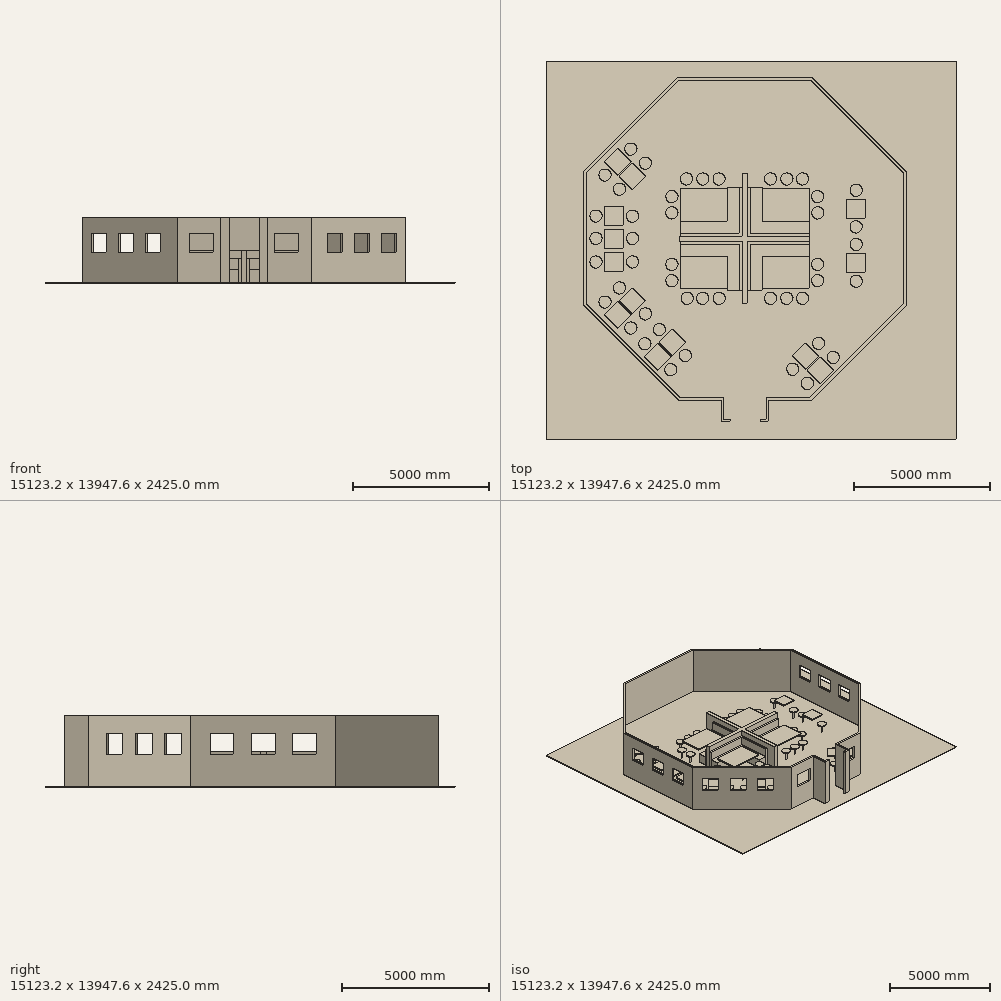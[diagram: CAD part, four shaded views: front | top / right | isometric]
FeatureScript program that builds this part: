
annotation { "Feature Type Name" : "Feature", "Feature Type Description" : "" }
export const myFeature = defineFeature(function(context is Context, id is Id, definition is map)
    precondition{}
    {
        {
            var Q0;
            Q0=qCreatedBy(makeId("Top.planeOp"),FACE);
            var sketch = newSketch(context, id + "F0", { "sketchPlane" : qUnion([Q0])});
            skLineSegment(sketch, "E0", {"start": v(-5845, -1966.08) * mm, "end": v(-2421.08, -5390) * mm});
            skLineSegment(sketch, "E1", {"start": v(-2421.08, -5390) * mm, "end": v(-780, -5390) * mm});
            skLineSegment(sketch, "E2", {"start": v(2421.08, -5390) * mm, "end": v(5845, -1966.08) * mm});
            skLineSegment(sketch, "E3", {"start": v(5845, -1966.08) * mm, "end": v(5845, 2876.08) * mm});
            skLineSegment(sketch, "E4", {"start": v(5845, 2876.08) * mm, "end": v(2421.08, 6300) * mm});
            skLineSegment(sketch, "E5", {"start": v(2421.08, 6300) * mm, "end": v(-2421.08, 6300) * mm});
            skLineSegment(sketch, "E6", {"start": v(-5955, -2011.64) * mm, "end": v(-2466.64, -5500) * mm});
            skLineSegment(sketch, "E7", {"start": v(-2466.64, -5500) * mm, "end": v(-870, -5500) * mm});
            skLineSegment(sketch, "E8", {"start": v(2466.64, -5500) * mm, "end": v(5955, -2011.64) * mm});
            skLineSegment(sketch, "E9", {"start": v(5955, -2011.64) * mm, "end": v(5955, 2921.64) * mm});
            skLineSegment(sketch, "E10", {"start": v(5955, 2921.64) * mm, "end": v(2466.64, 6410) * mm});
            skLineSegment(sketch, "E11", {"start": v(2466.64, 6410) * mm, "end": v(-2466.64, 6410) * mm});
            skLineSegment(sketch, "E12", {"start": v(-2466.64, 6410) * mm, "end": v(-5955, 2921.64) * mm});
            skLineSegment(sketch, "E13", {"start": v(-5955, 2921.64) * mm, "end": v(-5955, -2011.64) * mm});
            skLineSegment(sketch, "E14", {"start": v(-5845, 2876.08) * mm, "end": v(-5845, -1966.08) * mm});
            skLineSegment(sketch, "E15", {"start": v(4545, -1427.6) * mm, "end": v(4545, 2337.6) * mm});
            skLineSegment(sketch, "E16", {"start": v(4545, 2337.6) * mm, "end": v(3837.9, 3044.7) * mm});
            skLineSegment(sketch, "E17", {"start": v(4403.58, -1569.02) * mm, "end": v(4545, -1427.6) * mm});
            skLineSegment(sketch, "E18", {"start": v(5845, 2876.08) * mm, "end": v(4545, 2337.6) * mm});
            skLineSegment(sketch, "E19", {"start": v(5845, -1966.08) * mm, "end": v(4545, -1427.6) * mm});
            skLineSegment(sketch, "E20", {"start": v(4403.58, -1569.02) * mm, "end": v(5322.82, -2488.26) * mm});
            skLineSegment(sketch, "E21", {"start": v(3837.9, 3044.7) * mm, "end": v(4757.13, 3963.95) * mm});
            skLineSegment(sketch, "E22", {"start": v(-5845, 2876.08) * mm, "end": v(-5922.78, 2953.86) * mm});
            skLineSegment(sketch, "E23", {"start": v(-2421.08, 6300) * mm, "end": v(-5845, 2876.08) * mm});
            skLineSegment(sketch, "E24", {"start": v(870, -5500) * mm, "end": v(870, -6300) * mm});
            skLineSegment(sketch, "E25", {"start": v(-870, -5500) * mm, "end": v(-870, -6300) * mm});
            skLineSegment(sketch, "E26", {"start": v(-870, -6300) * mm, "end": v(870, -6300) * mm});
            skLineSegment(sketch, "E27", {"start": v(-780, -5390) * mm, "end": v(-780, -6210) * mm});
            skLineSegment(sketch, "E28", {"start": v(-780, -6210) * mm, "end": v(780, -6210) * mm});
            skLineSegment(sketch, "E29", {"start": v(780, -5390) * mm, "end": v(780, -6210) * mm});
            skLineSegment(sketch, "E30", {"start": v(550, -6210) * mm, "end": v(550, -6300) * mm});
            skLineSegment(sketch, "E31", {"start": v(-550, -6210) * mm, "end": v(-550, -6300) * mm});
            skLineSegment(sketch, "E32", {"start": v(870, -5500) * mm, "end": v(2466.64, -5500) * mm});
            skLineSegment(sketch, "E33", {"start": v(780, -5390) * mm, "end": v(2421.08, -5390) * mm});
            skLineSegment(sketch, "E34", {"start": v(1120, -5500) * mm, "end": v(1120, -5390) * mm});
            skLineSegment(sketch, "E35", {"start": v(2020, -5500) * mm, "end": v(2020, -5390) * mm});
            skLineSegment(sketch, "E36", {"start": v(-1120, -5500) * mm, "end": v(-1120, -5390) * mm});
            skLineSegment(sketch, "E37", {"start": v(-2020, -5500) * mm, "end": v(-2020, -5390) * mm});
            skLineSegment(sketch, "E38", {"start": v(-4069.4, -3897.24) * mm, "end": v(-3991.62, -3819.46) * mm});
            skLineSegment(sketch, "E39", {"start": v(-4635.08, -3331.56) * mm, "end": v(-4557.3, -3253.78) * mm});
            skLineSegment(sketch, "E40", {"start": v(-3645.14, -4321.5) * mm, "end": v(-3567.35, -4243.72) * mm});
            skLineSegment(sketch, "E41", {"start": v(-5059.35, -2907.3) * mm, "end": v(-4981.57, -2829.51) * mm});
            skLineSegment(sketch, "E42", {"start": v(-3079.45, -4887.2) * mm, "end": v(-3001.67, -4809.4) * mm});
            skLineSegment(sketch, "E43", {"start": v(-5625.03, -2341.6) * mm, "end": v(-5547.25, -2263.83) * mm});
            skLineSegment(sketch, "E44", {"start": v(4069.4, -3897.24) * mm, "end": v(3991.62, -3819.46) * mm});
            skLineSegment(sketch, "E45", {"start": v(4635.08, -3331.56) * mm, "end": v(4557.3, -3253.78) * mm});
            skLineSegment(sketch, "E46", {"start": v(3645.14, -4321.5) * mm, "end": v(3567.35, -4243.72) * mm});
            skLineSegment(sketch, "E47", {"start": v(5059.35, -2907.3) * mm, "end": v(4981.57, -2829.51) * mm});
            skLineSegment(sketch, "E48", {"start": v(3079.45, -4887.2) * mm, "end": v(3001.67, -4809.4) * mm});
            skLineSegment(sketch, "E49", {"start": v(5625.03, -2341.6) * mm, "end": v(5547.25, -2263.83) * mm});
            skLineSegment(sketch, "E50", {"start": v(-4069.4, 4807.24) * mm, "end": v(-3991.62, 4729.46) * mm});
            skLineSegment(sketch, "E51", {"start": v(-4635.08, 4241.56) * mm, "end": v(-4557.3, 4163.78) * mm});
            skLineSegment(sketch, "E52", {"start": v(-3645.14, 5231.5) * mm, "end": v(-3567.35, 5153.72) * mm});
            skLineSegment(sketch, "E53", {"start": v(-5059.35, 3817.3) * mm, "end": v(-4981.57, 3739.51) * mm});
            skLineSegment(sketch, "E54", {"start": v(-3079.45, 5797.2) * mm, "end": v(-3001.67, 5719.4) * mm});
            skLineSegment(sketch, "E55", {"start": v(-5625.03, 3251.6) * mm, "end": v(-5547.25, 3173.83) * mm});
            skLineSegment(sketch, "E56", {"start": v(-5845, 55) * mm, "end": v(-5955, 55) * mm});
            skLineSegment(sketch, "E57", {"start": v(-5845, 855) * mm, "end": v(-5955, 855) * mm});
            skLineSegment(sketch, "E58", {"start": v(-5845, -545) * mm, "end": v(-5955, -545) * mm});
            skLineSegment(sketch, "E59", {"start": v(-5845, 1455) * mm, "end": v(-5955, 1455) * mm});
            skLineSegment(sketch, "E60", {"start": v(-5845, -1345) * mm, "end": v(-5955, -1345) * mm});
            skLineSegment(sketch, "E61", {"start": v(-5845, 2255) * mm, "end": v(-5955, 2255) * mm});
            skLineSegment(sketch, "E62", {"start": v(5845, 55) * mm, "end": v(5955, 55) * mm});
            skLineSegment(sketch, "E63", {"start": v(5845, 855) * mm, "end": v(5955, 855) * mm});
            skLineSegment(sketch, "E64", {"start": v(5845, -545) * mm, "end": v(5955, -545) * mm});
            skLineSegment(sketch, "E65", {"start": v(5845, 1455) * mm, "end": v(5955, 1455) * mm});
            skLineSegment(sketch, "E66", {"start": v(5845, -1345) * mm, "end": v(5955, -1345) * mm});
            skLineSegment(sketch, "E67", {"start": v(5845, 2255) * mm, "end": v(5955, 2255) * mm});
            skLineSegment(sketch, "E68", {"start": v(0, 6300) * mm, "end": v(0, 6410) * mm});
            skLineSegment(sketch, "E69", {"start": v(-5955, 1855) * mm, "end": v(-5955, -945) * mm});
            skLineSegment(sketch, "E70", {"start": v(3748.03, -90.66) * mm, "end": v(4448.03, -90.66) * mm});
            skLineSegment(sketch, "E71", {"start": v(4448.03, -90.66) * mm, "end": v(4448.03, -790.66) * mm});
            skLineSegment(sketch, "E72", {"start": v(4448.03, -790.66) * mm, "end": v(3748.03, -790.66) * mm});
            skLineSegment(sketch, "E73", {"start": v(3748.03, -790.66) * mm, "end": v(3748.03, -90.66) * mm});
            skCircle(sketch, "E74", {"center": v(4098.03, 234.34) * mm, "radius": 225 * mm});
            skCircle(sketch, "E75", {"center": v(4098.03, -1115.66) * mm, "radius": 225 * mm});
            skLineSegment(sketch, "E76", {"start": v(-4690.36, -2860.67) * mm, "end": v(-4195.38, -2365.7) * mm});
            skLineSegment(sketch, "E77", {"start": v(-4195.38, -2365.7) * mm, "end": v(-4690.36, -1870.72) * mm});
            skLineSegment(sketch, "E78", {"start": v(-4690.36, -1870.72) * mm, "end": v(-5185.33, -2365.7) * mm});
            skLineSegment(sketch, "E79", {"start": v(-5185.33, -2365.7) * mm, "end": v(-4690.36, -2860.67) * mm});
            skCircle(sketch, "E80", {"center": v(-4213.06, -2843) * mm, "radius": 225 * mm});
            skCircle(sketch, "E81", {"center": v(-5167.65, -1888.4) * mm, "radius": 225 * mm});
            skLineSegment(sketch, "E82", {"start": v(-4152.39, -2339.78) * mm, "end": v(-3657.41, -1844.8) * mm});
            skLineSegment(sketch, "E83", {"start": v(-3657.41, -1844.8) * mm, "end": v(-4152.39, -1349.83) * mm});
            skLineSegment(sketch, "E84", {"start": v(-4152.39, -1349.83) * mm, "end": v(-4647.36, -1844.8) * mm});
            skLineSegment(sketch, "E85", {"start": v(-4647.36, -1844.8) * mm, "end": v(-4152.39, -2339.78) * mm});
            skCircle(sketch, "E86", {"center": v(-3675.09, -2322.1) * mm, "radius": 225 * mm});
            skCircle(sketch, "E87", {"center": v(-4629.68, -1367.51) * mm, "radius": 225 * mm});
            skLineSegment(sketch, "E88", {"start": v(-5174.43, -57.81) * mm, "end": v(-5174.43, -757.81) * mm});
            skLineSegment(sketch, "E89", {"start": v(-5174.43, -757.81) * mm, "end": v(-4474.43, -757.81) * mm});
            skLineSegment(sketch, "E90", {"start": v(-4474.43, -757.81) * mm, "end": v(-4474.43, -57.81) * mm});
            skLineSegment(sketch, "E91", {"start": v(-4474.43, -57.81) * mm, "end": v(-5174.43, -57.81) * mm});
            skCircle(sketch, "E92", {"center": v(-4149.43, -407.81) * mm, "radius": 225 * mm});
            skLineSegment(sketch, "E93", {"start": v(-5174.43, 809.45) * mm, "end": v(-5174.43, 109.45) * mm});
            skLineSegment(sketch, "E94", {"start": v(-5174.43, 109.45) * mm, "end": v(-4474.43, 109.45) * mm});
            skLineSegment(sketch, "E95", {"start": v(-4474.43, 109.45) * mm, "end": v(-4474.43, 809.45) * mm});
            skLineSegment(sketch, "E96", {"start": v(-4474.43, 809.45) * mm, "end": v(-5174.43, 809.45) * mm});
            skCircle(sketch, "E97", {"center": v(-4149.43, 459.45) * mm, "radius": 225 * mm});
            skLineSegment(sketch, "E98", {"start": v(-5174.43, 1632.23) * mm, "end": v(-5174.43, 932.23) * mm});
            skLineSegment(sketch, "E99", {"start": v(-5174.43, 932.23) * mm, "end": v(-4474.43, 932.23) * mm});
            skLineSegment(sketch, "E100", {"start": v(-4474.43, 932.23) * mm, "end": v(-4474.43, 1632.23) * mm});
            skLineSegment(sketch, "E101", {"start": v(-4474.43, 1632.23) * mm, "end": v(-5174.43, 1632.23) * mm});
            skCircle(sketch, "E102", {"center": v(-4149.43, 1282.23) * mm, "radius": 225 * mm});
            skLineSegment(sketch, "E103", {"start": v(2776.75, -4904.66) * mm, "end": v(2281.78, -4409.68) * mm});
            skLineSegment(sketch, "E104", {"start": v(2281.78, -4409.68) * mm, "end": v(2776.75, -3914.7) * mm});
            skLineSegment(sketch, "E105", {"start": v(2776.75, -3914.7) * mm, "end": v(3271.73, -4409.68) * mm});
            skLineSegment(sketch, "E106", {"start": v(3271.73, -4409.68) * mm, "end": v(2776.75, -4904.66) * mm});
            skCircle(sketch, "E107", {"center": v(2299.45, -4886.98) * mm, "radius": 225 * mm});
            skCircle(sketch, "E108", {"center": v(3254.05, -3932.39) * mm, "radius": 225 * mm});
            skLineSegment(sketch, "E109", {"start": v(2238.78, -4383.77) * mm, "end": v(1743.8, -3888.8) * mm});
            skLineSegment(sketch, "E110", {"start": v(1743.8, -3888.8) * mm, "end": v(2238.78, -3393.82) * mm});
            skLineSegment(sketch, "E111", {"start": v(2238.78, -3393.82) * mm, "end": v(2733.76, -3888.8) * mm});
            skLineSegment(sketch, "E112", {"start": v(2733.76, -3888.8) * mm, "end": v(2238.78, -4383.77) * mm});
            skCircle(sketch, "E113", {"center": v(1761.49, -4366.09) * mm, "radius": 225 * mm});
            skCircle(sketch, "E114", {"center": v(2716.08, -3411.5) * mm, "radius": 225 * mm});
            skLineSegment(sketch, "E115", {"start": v(780, -5390) * mm, "end": v(-780, -5390) * mm});
            skLineSegment(sketch, "E116", {"start": v(-1375, -3565) * mm, "end": v(1375, -3565) * mm});
            skLineSegment(sketch, "E117", {"start": v(-1375, -3565) * mm, "end": v(-1375, -5390) * mm});
            skLineSegment(sketch, "E118", {"start": v(1375, -3565) * mm, "end": v(1375, -5390) * mm});
            skLineSegment(sketch, "E119", {"start": v(-1445, -3495) * mm, "end": v(-1445, -5390) * mm});
            skLineSegment(sketch, "E120", {"start": v(-1445, -3495) * mm, "end": v(1445, -3495) * mm});
            skLineSegment(sketch, "E121", {"start": v(1445, -3495) * mm, "end": v(1445, -5390) * mm});
            skLineSegment(sketch, "E122", {"start": v(91.05, 551.97) * mm, "end": v(2391.05, 551.97) * mm});
            skLineSegment(sketch, "E123", {"start": v(2391.05, 551.97) * mm, "end": v(2391.05, 351.97) * mm});
            skLineSegment(sketch, "E124", {"start": v(2391.05, 351.97) * mm, "end": v(91.05, 351.97) * mm});
            skLineSegment(sketch, "E125", {"start": v(-108.95, 551.97) * mm, "end": v(-108.95, 2855) * mm});
            skLineSegment(sketch, "E126", {"start": v(-108.95, 2855) * mm, "end": v(91.05, 2855) * mm});
            skLineSegment(sketch, "E127", {"start": v(91.05, 2855) * mm, "end": v(91.05, 551.97) * mm});
            skLineSegment(sketch, "E128", {"start": v(-108.95, 351.97) * mm, "end": v(-2306.97, 351.97) * mm});
            skLineSegment(sketch, "E129", {"start": v(-108.95, 2351.97) * mm, "end": v(-108.95, 551.97) * mm});
            skLineSegment(sketch, "E130", {"start": v(-208.95, 651.97) * mm, "end": v(-208.95, 2303.17) * mm});
            skLineSegment(sketch, "E131", {"start": v(-208.95, 2351.97) * mm, "end": v(-108.95, 2351.97) * mm});
            skLineSegment(sketch, "E132", {"start": v(-2381.97, 651.97) * mm, "end": v(-208.95, 651.97) * mm});
            skLineSegment(sketch, "E133", {"start": v(-108.95, 551.97) * mm, "end": v(-2381.97, 551.97) * mm});
            skLineSegment(sketch, "E134", {"start": v(-2381.97, 551.97) * mm, "end": v(-2381.97, 651.97) * mm});
            skLineSegment(sketch, "E135", {"start": v(-208.95, 2351.97) * mm, "end": v(-208.95, 651.97) * mm});
            skLineSegment(sketch, "E136", {"start": v(-658.95, 1101.97) * mm, "end": v(-658.95, 2351.97) * mm});
            skLineSegment(sketch, "E137", {"start": v(-658.95, 2351.97) * mm, "end": v(-208.95, 2351.97) * mm});
            skLineSegment(sketch, "E138", {"start": v(-208.95, 651.97) * mm, "end": v(-2381.97, 651.97) * mm});
            skLineSegment(sketch, "E139", {"start": v(-2381.97, 651.97) * mm, "end": v(-2381.97, 1101.97) * mm});
            skLineSegment(sketch, "E140", {"start": v(-2381.97, 1101.97) * mm, "end": v(-658.95, 1101.97) * mm});
            skLineSegment(sketch, "E141", {"start": v(91.05, 2659.09) * mm, "end": v(91.05, 551.97) * mm});
            skCircle(sketch, "E142", {"center": v(-416.78, 1951.97) * mm, "radius": 125 * mm});
            skCircle(sketch, "E143", {"center": v(-420.43, 1351.97) * mm, "radius": 125 * mm});
            skCircle(sketch, "E144", {"center": v(-908.95, 863.44) * mm, "radius": 125 * mm});
            skCircle(sketch, "E145", {"center": v(-1508.95, 859.8) * mm, "radius": 125 * mm});
            skCircle(sketch, "E146", {"center": v(-2699.02, 1401.97) * mm, "radius": 225 * mm});
            skCircle(sketch, "E147", {"center": v(-2699.02, 2001.97) * mm, "radius": 225 * mm});
            skCircle(sketch, "E148", {"center": v(-1558.95, 2653.44) * mm, "radius": 225 * mm});
            skCircle(sketch, "E149", {"center": v(-958.95, 2653.44) * mm, "radius": 225 * mm});
            skLineSegment(sketch, "E150", {"start": v(-2381.97, 2301.97) * mm, "end": v(-2381.97, 1101.97) * mm});
            skLineSegment(sketch, "E151", {"start": v(-658.95, 1101.97) * mm, "end": v(-658.95, 2301.97) * mm});
            skLineSegment(sketch, "E152", {"start": v(-658.95, 2301.97) * mm, "end": v(-2381.97, 2301.97) * mm});
            skLineSegment(sketch, "E153", {"start": v(-3218.24, -4399.5) * mm, "end": v(-2723.26, -3904.53) * mm});
            skLineSegment(sketch, "E154", {"start": v(-2723.26, -3904.53) * mm, "end": v(-3218.24, -3409.56) * mm});
            skLineSegment(sketch, "E155", {"start": v(-3218.24, -3409.56) * mm, "end": v(-3713.2, -3904.53) * mm});
            skLineSegment(sketch, "E156", {"start": v(-3713.2, -3904.53) * mm, "end": v(-3218.24, -4399.5) * mm});
            skCircle(sketch, "E157", {"center": v(-2740.94, -4381.83) * mm, "radius": 225 * mm});
            skLineSegment(sketch, "E158", {"start": v(-2680.27, -3878.62) * mm, "end": v(-2185.3, -3383.64) * mm});
            skLineSegment(sketch, "E159", {"start": v(-2185.3, -3383.64) * mm, "end": v(-2680.27, -2888.67) * mm});
            skLineSegment(sketch, "E160", {"start": v(-2680.27, -2888.67) * mm, "end": v(-3175.24, -3383.64) * mm});
            skLineSegment(sketch, "E161", {"start": v(-3175.24, -3383.64) * mm, "end": v(-2680.27, -3878.62) * mm});
            skCircle(sketch, "E162", {"center": v(-2202.97, -3860.94) * mm, "radius": 225 * mm});
            skCircle(sketch, "E163", {"center": v(-3157.56, -2906.34) * mm, "radius": 225 * mm});
            skCircle(sketch, "E164", {"center": v(-3695.53, -3427.23) * mm, "radius": 225 * mm});
            skCircle(sketch, "E165", {"center": v(-5499.43, -407.81) * mm, "radius": 225 * mm});
            skCircle(sketch, "E166", {"center": v(-5499.43, 459.45) * mm, "radius": 225 * mm});
            skCircle(sketch, "E167", {"center": v(-5499.43, 1282.23) * mm, "radius": 225 * mm});
            skLineSegment(sketch, "E168", {"start": v(-4690.36, 3770.67) * mm, "end": v(-4195.38, 3275.7) * mm});
            skLineSegment(sketch, "E169", {"start": v(-4195.38, 3275.7) * mm, "end": v(-4690.36, 2780.72) * mm});
            skLineSegment(sketch, "E170", {"start": v(-4690.36, 2780.72) * mm, "end": v(-5185.33, 3275.7) * mm});
            skLineSegment(sketch, "E171", {"start": v(-5185.33, 3275.7) * mm, "end": v(-4690.36, 3770.67) * mm});
            skCircle(sketch, "E172", {"center": v(-4213.06, 3753) * mm, "radius": 225 * mm});
            skLineSegment(sketch, "E173", {"start": v(-4152.39, 3249.78) * mm, "end": v(-3657.41, 2754.8) * mm});
            skLineSegment(sketch, "E174", {"start": v(-3657.41, 2754.8) * mm, "end": v(-4152.39, 2259.83) * mm});
            skLineSegment(sketch, "E175", {"start": v(-4152.39, 2259.83) * mm, "end": v(-4647.36, 2754.8) * mm});
            skLineSegment(sketch, "E176", {"start": v(-4647.36, 2754.8) * mm, "end": v(-4152.39, 3249.78) * mm});
            skCircle(sketch, "E177", {"center": v(-3675.09, 3232.1) * mm, "radius": 225 * mm});
            skCircle(sketch, "E178", {"center": v(-5167.65, 2798.4) * mm, "radius": 225 * mm});
            skCircle(sketch, "E179", {"center": v(-4629.68, 2277.51) * mm, "radius": 225 * mm});
            skLineSegment(sketch, "E180", {"start": v(3748.03, 1910.71) * mm, "end": v(4448.03, 1910.71) * mm});
            skLineSegment(sketch, "E181", {"start": v(4448.03, 1910.71) * mm, "end": v(4448.03, 1210.71) * mm});
            skLineSegment(sketch, "E182", {"start": v(4448.03, 1210.71) * mm, "end": v(3748.03, 1210.71) * mm});
            skLineSegment(sketch, "E183", {"start": v(3748.03, 1210.71) * mm, "end": v(3748.03, 1910.71) * mm});
            skCircle(sketch, "E184", {"center": v(4098.03, 2235.71) * mm, "radius": 225 * mm});
            skCircle(sketch, "E185", {"center": v(4098.03, 885.71) * mm, "radius": 225 * mm});
            skCircle(sketch, "E186", {"center": v(-2108.95, 859.8) * mm, "radius": 125 * mm});
            skCircle(sketch, "E187", {"center": v(-2158.94, 2653.14) * mm, "radius": 225 * mm});
            skLineSegment(sketch, "E188", {"start": v(-108.95, 351.97) * mm, "end": v(-2408.95, 351.97) * mm});
            skLineSegment(sketch, "E189", {"start": v(-2408.95, 351.97) * mm, "end": v(-2408.95, 551.97) * mm});
            skLineSegment(sketch, "E190", {"start": v(-2408.95, 551.97) * mm, "end": v(-108.95, 551.97) * mm});
            skLineSegment(sketch, "E191", {"start": v(91.05, 351.97) * mm, "end": v(91.05, -1945) * mm});
            skLineSegment(sketch, "E192", {"start": v(91.05, -1945) * mm, "end": v(-108.95, -1945) * mm});
            skLineSegment(sketch, "E193", {"start": v(-108.95, -1945) * mm, "end": v(-108.95, 351.97) * mm});
            skLineSegment(sketch, "E194", {"start": v(191.05, 651.97) * mm, "end": v(191.05, 2303.17) * mm});
            skLineSegment(sketch, "E195", {"start": v(191.05, 2351.97) * mm, "end": v(91.05, 2351.97) * mm});
            skLineSegment(sketch, "E196", {"start": v(2364.06, 651.97) * mm, "end": v(191.05, 651.97) * mm});
            skLineSegment(sketch, "E197", {"start": v(2364.06, 551.97) * mm, "end": v(2364.06, 651.97) * mm});
            skLineSegment(sketch, "E198", {"start": v(191.05, 2351.97) * mm, "end": v(191.05, 651.97) * mm});
            skLineSegment(sketch, "E199", {"start": v(641.05, 1101.97) * mm, "end": v(641.05, 2351.97) * mm});
            skLineSegment(sketch, "E200", {"start": v(641.05, 2351.97) * mm, "end": v(191.05, 2351.97) * mm});
            skLineSegment(sketch, "E201", {"start": v(191.05, 651.97) * mm, "end": v(2364.06, 651.97) * mm});
            skLineSegment(sketch, "E202", {"start": v(2364.06, 651.97) * mm, "end": v(2364.06, 1101.97) * mm});
            skLineSegment(sketch, "E203", {"start": v(2364.06, 1101.97) * mm, "end": v(641.05, 1101.97) * mm});
            skCircle(sketch, "E204", {"center": v(398.87, 1951.97) * mm, "radius": 125 * mm});
            skCircle(sketch, "E205", {"center": v(402.52, 1351.97) * mm, "radius": 125 * mm});
            skCircle(sketch, "E206", {"center": v(891.05, 863.44) * mm, "radius": 125 * mm});
            skCircle(sketch, "E207", {"center": v(1491.05, 859.8) * mm, "radius": 125 * mm});
            skCircle(sketch, "E208", {"center": v(2681.11, 1401.97) * mm, "radius": 225 * mm});
            skCircle(sketch, "E209", {"center": v(2681.11, 2001.97) * mm, "radius": 225 * mm});
            skCircle(sketch, "E210", {"center": v(1541.05, 2653.44) * mm, "radius": 225 * mm});
            skCircle(sketch, "E211", {"center": v(941.05, 2653.44) * mm, "radius": 225 * mm});
            skLineSegment(sketch, "E212", {"start": v(2364.06, 2301.97) * mm, "end": v(2364.06, 1101.97) * mm});
            skLineSegment(sketch, "E213", {"start": v(641.05, 1101.97) * mm, "end": v(641.05, 2301.97) * mm});
            skLineSegment(sketch, "E214", {"start": v(641.05, 2301.97) * mm, "end": v(2364.06, 2301.97) * mm});
            skCircle(sketch, "E215", {"center": v(2091.05, 859.8) * mm, "radius": 125 * mm});
            skCircle(sketch, "E216", {"center": v(2119.43, 2653.44) * mm, "radius": 225 * mm});
            skLineSegment(sketch, "E217", {"start": v(-208.95, 251.97) * mm, "end": v(-208.95, -1399.23) * mm});
            skLineSegment(sketch, "E218", {"start": v(-2378.97, 251.97) * mm, "end": v(-208.95, 251.97) * mm});
            skLineSegment(sketch, "E219", {"start": v(-208.95, -1449.23) * mm, "end": v(-208.95, 251.97) * mm});
            skLineSegment(sketch, "E220", {"start": v(-658.95, -198.03) * mm, "end": v(-658.95, -1449.23) * mm});
            skLineSegment(sketch, "E221", {"start": v(-658.95, -1449.23) * mm, "end": v(-208.95, -1449.23) * mm});
            skLineSegment(sketch, "E222", {"start": v(-208.95, 251.97) * mm, "end": v(-2378.97, 251.97) * mm});
            skLineSegment(sketch, "E223", {"start": v(-2378.97, 251.97) * mm, "end": v(-2378.97, -198.03) * mm});
            skLineSegment(sketch, "E224", {"start": v(-2378.97, -198.03) * mm, "end": v(-658.95, -198.03) * mm});
            skCircle(sketch, "E225", {"center": v(-416.78, -1048.03) * mm, "radius": 125 * mm});
            skCircle(sketch, "E226", {"center": v(-420.43, -448.03) * mm, "radius": 125 * mm});
            skCircle(sketch, "E227", {"center": v(-908.95, 40.5) * mm, "radius": 125 * mm});
            skCircle(sketch, "E228", {"center": v(-1508.95, 44.14) * mm, "radius": 125 * mm});
            skCircle(sketch, "E229", {"center": v(-2699.02, -498.03) * mm, "radius": 225 * mm});
            skCircle(sketch, "E230", {"center": v(-2699.02, -1098.03) * mm, "radius": 225 * mm});
            skCircle(sketch, "E231", {"center": v(-1558.95, -1749.5) * mm, "radius": 225 * mm});
            skCircle(sketch, "E232", {"center": v(-958.95, -1749.5) * mm, "radius": 225 * mm});
            skLineSegment(sketch, "E233", {"start": v(-2378.97, -1398.03) * mm, "end": v(-2378.97, -198.03) * mm});
            skLineSegment(sketch, "E234", {"start": v(-658.95, -198.03) * mm, "end": v(-658.95, -1398.03) * mm});
            skLineSegment(sketch, "E235", {"start": v(-658.95, -1398.03) * mm, "end": v(-2378.97, -1398.03) * mm});
            skCircle(sketch, "E236", {"center": v(-2108.95, 44.14) * mm, "radius": 125 * mm});
            skCircle(sketch, "E237", {"center": v(-2137.34, -1749.5) * mm, "radius": 225 * mm});
            skLineSegment(sketch, "E238", {"start": v(-2378.97, 351.97) * mm, "end": v(-2378.97, 251.97) * mm});
            skLineSegment(sketch, "E239", {"start": v(-208.95, -1449.23) * mm, "end": v(-108.95, -1449.23) * mm});
            skLineSegment(sketch, "E240", {"start": v(191.05, 251.97) * mm, "end": v(191.05, -1399.23) * mm});
            skLineSegment(sketch, "E241", {"start": v(2364.06, 251.97) * mm, "end": v(191.05, 251.97) * mm});
            skLineSegment(sketch, "E242", {"start": v(191.05, -1449.23) * mm, "end": v(191.05, 251.97) * mm});
            skLineSegment(sketch, "E243", {"start": v(641.05, -198.03) * mm, "end": v(641.05, -1449.23) * mm});
            skLineSegment(sketch, "E244", {"start": v(641.05, -1449.23) * mm, "end": v(191.05, -1449.23) * mm});
            skLineSegment(sketch, "E245", {"start": v(191.05, 251.97) * mm, "end": v(2364.06, 251.97) * mm});
            skLineSegment(sketch, "E246", {"start": v(2364.06, 251.97) * mm, "end": v(2364.06, -198.03) * mm});
            skLineSegment(sketch, "E247", {"start": v(2364.06, -198.03) * mm, "end": v(641.05, -198.03) * mm});
            skCircle(sketch, "E248", {"center": v(398.87, -1048.03) * mm, "radius": 125 * mm});
            skCircle(sketch, "E249", {"center": v(402.52, -448.03) * mm, "radius": 125 * mm});
            skCircle(sketch, "E250", {"center": v(891.05, 40.5) * mm, "radius": 125 * mm});
            skCircle(sketch, "E251", {"center": v(1491.05, 44.14) * mm, "radius": 125 * mm});
            skCircle(sketch, "E252", {"center": v(2681.11, -498.03) * mm, "radius": 225 * mm});
            skCircle(sketch, "E253", {"center": v(2681.11, -1098.03) * mm, "radius": 225 * mm});
            skCircle(sketch, "E254", {"center": v(1541.05, -1749.5) * mm, "radius": 225 * mm});
            skCircle(sketch, "E255", {"center": v(941.05, -1749.5) * mm, "radius": 225 * mm});
            skLineSegment(sketch, "E256", {"start": v(2364.06, -1398.03) * mm, "end": v(2364.06, -198.03) * mm});
            skLineSegment(sketch, "E257", {"start": v(641.05, -198.03) * mm, "end": v(641.05, -1398.03) * mm});
            skLineSegment(sketch, "E258", {"start": v(641.05, -1398.03) * mm, "end": v(2364.06, -1398.03) * mm});
            skCircle(sketch, "E259", {"center": v(2091.05, 44.14) * mm, "radius": 125 * mm});
            skCircle(sketch, "E260", {"center": v(2119.43, -1749.5) * mm, "radius": 225 * mm});
            skLineSegment(sketch, "E261", {"start": v(2364.06, 351.97) * mm, "end": v(2364.06, 251.97) * mm});
            skLineSegment(sketch, "E262", {"start": v(191.05, -1449.23) * mm, "end": v(91.05, -1449.23) * mm});
            skSolve(sketch);
        }
        {
            var Q0;
            Q0=qCreatedBy(makeId("Top.planeOp"),FACE);
            var sketch = newSketch(context, id + "F1", { "sketchPlane" : qUnion([Q0])});
            skSolve(sketch);
        }
        {
            var Q0;
            Q0 = qSketchRegion(id + "F1", true);
            var Q1;
            {var subQ3=sQuery(id+"F0.wireOp",EDGE,"E37");Q1=makeQuery(id+"F0.imprint","IMPRINT",FACE,{"disambiguationData":[TD([[makeQuery(id+"F0.imprint","IMPRINT",EDGE,{"derivedFrom":subQ3}),1.0]])]});}
            var Q2;
            {var subQ0=sQuery(id+"F0.wireOp",EDGE,"E38");Q2=makeQuery(id+"F0.imprint","IMPRINT",FACE,{"disambiguationData":[TD([[makeQuery(id+"F0.imprint","IMPRINT",EDGE,{"derivedFrom":subQ0}),-1.0]])]});}
            var Q3;
            {var subQ0=sQuery(id+"F0.wireOp",EDGE,"E39");Q3=makeQuery(id+"F0.imprint","IMPRINT",FACE,{"disambiguationData":[TD([[makeQuery(id+"F0.imprint","IMPRINT",EDGE,{"derivedFrom":subQ0}),1.0]])]});}
            var Q4;
            {var subQ7=sQuery(id+"F0.wireOp",EDGE,"E43");Q4=makeQuery(id+"F0.imprint","IMPRINT",FACE,{"disambiguationData":[TD([[makeQuery(id+"F0.imprint","IMPRINT",EDGE,{"derivedFrom":subQ7}),1.0]])]});}
            var Q5;
            {var subQ0=sQuery(id+"F0.wireOp",EDGE,"E56");Q5=makeQuery(id+"F0.imprint","IMPRINT",FACE,{"disambiguationData":[TD([[makeQuery(id+"F0.imprint","IMPRINT",EDGE,{"derivedFrom":subQ0}),1.0]])]});}
            var Q6;
            {var subQ0=sQuery(id+"F0.wireOp",EDGE,"E57");Q6=makeQuery(id+"F0.imprint","IMPRINT",FACE,{"disambiguationData":[TD([[makeQuery(id+"F0.imprint","IMPRINT",EDGE,{"derivedFrom":subQ0}),-1.0]])]});}
            var Q7;
            {var subQ0=sQuery(id+"F0.wireOp",EDGE,"E22");Q7=makeQuery(id+"F0.imprint","IMPRINT",FACE,{"disambiguationData":[TD([[makeQuery(id+"F0.imprint","IMPRINT",EDGE,{"derivedFrom":subQ0}),1.0]])]});}
            var Q8;
            {var subQ0=sQuery(id+"F0.wireOp",EDGE,"E22");Q8=makeQuery(id+"F0.imprint","IMPRINT",FACE,{"disambiguationData":[TD([[makeQuery(id+"F0.imprint","IMPRINT",EDGE,{"derivedFrom":subQ0}),-1.0]])]});}
            var Q9;
            {var subQ0=sQuery(id+"F0.wireOp",EDGE,"E51");Q9=makeQuery(id+"F0.imprint","IMPRINT",FACE,{"disambiguationData":[TD([[makeQuery(id+"F0.imprint","IMPRINT",EDGE,{"derivedFrom":subQ0}),-1.0]])]});}
            var Q10;
            {var subQ0=sQuery(id+"F0.wireOp",EDGE,"E50");Q10=makeQuery(id+"F0.imprint","IMPRINT",FACE,{"disambiguationData":[TD([[makeQuery(id+"F0.imprint","IMPRINT",EDGE,{"derivedFrom":subQ0}),1.0]])]});}
            var Q11;
            {var subQ3=sQuery(id+"F0.wireOp",EDGE,"E54");Q11=makeQuery(id+"F0.imprint","IMPRINT",FACE,{"disambiguationData":[TD([[makeQuery(id+"F0.imprint","IMPRINT",EDGE,{"derivedFrom":subQ3}),1.0]])]});}
            var Q12;
            {var subQ8=sQuery(id+"F0.wireOp",EDGE,"E10");Q12=makeQuery(id+"F0.imprint","IMPRINT",FACE,{"disambiguationData":[TD([[makeQuery(id+"F0.imprint","IMPRINT",EDGE,{"derivedFrom":subQ8}),1.0]])]});}
            var Q13;
            {var subQ1=sQuery(id+"F0.wireOp",EDGE,"E25");Q13=makeQuery(id+"F0.imprint","IMPRINT",FACE,{"disambiguationData":[TD([[makeQuery(id+"F0.imprint","IMPRINT",EDGE,{"derivedFrom":subQ1}),1.0]])]});}
            var Q14;
            {var subQ5=sQuery(id+"F0.wireOp",EDGE,"E24");Q14=makeQuery(id+"F0.imprint","IMPRINT",FACE,{"disambiguationData":[TD([[makeQuery(id+"F0.imprint","IMPRINT",EDGE,{"derivedFrom":subQ5}),-1.0]])]});}
            var Q15;
            {var subQ3=sQuery(id+"F0.wireOp",EDGE,"E35");Q15=makeQuery(id+"F0.imprint","IMPRINT",FACE,{"disambiguationData":[TD([[makeQuery(id+"F0.imprint","IMPRINT",EDGE,{"derivedFrom":subQ3}),-1.0]])]});}
            var Q16;
            {var subQ0=sQuery(id+"F0.wireOp",EDGE,"E44");Q16=makeQuery(id+"F0.imprint","IMPRINT",FACE,{"disambiguationData":[TD([[makeQuery(id+"F0.imprint","IMPRINT",EDGE,{"derivedFrom":subQ0}),1.0]])]});}
            var Q17;
            {var subQ0=sQuery(id+"F0.wireOp",EDGE,"E45");Q17=makeQuery(id+"F0.imprint","IMPRINT",FACE,{"disambiguationData":[TD([[makeQuery(id+"F0.imprint","IMPRINT",EDGE,{"derivedFrom":subQ0}),-1.0]])]});}
            var Q18;
            {var subQ4=sQuery(id+"F0.wireOp",EDGE,"E49");Q18=makeQuery(id+"F0.imprint","IMPRINT",FACE,{"disambiguationData":[TD([[makeQuery(id+"F0.imprint","IMPRINT",EDGE,{"derivedFrom":subQ4}),-1.0]])]});}
            var Q19;
            {var subQ0=sQuery(id+"F0.wireOp",EDGE,"E62");Q19=makeQuery(id+"F0.imprint","IMPRINT",FACE,{"disambiguationData":[TD([[makeQuery(id+"F0.imprint","IMPRINT",EDGE,{"derivedFrom":subQ0}),-1.0]])]});}
            var Q20;
            {var subQ0=sQuery(id+"F0.wireOp",EDGE,"E63");Q20=makeQuery(id+"F0.imprint","IMPRINT",FACE,{"disambiguationData":[TD([[makeQuery(id+"F0.imprint","IMPRINT",EDGE,{"derivedFrom":subQ0}),1.0]])]});}
            extrude(context, id + "F2", {"entities" : qUnion([Q0, Q1, Q2, Q3, Q4, Q5, Q6, Q7, Q8, Q9, Q10, Q11, Q12, Q13, Q14, Q15, Q16, Q17, Q18, Q19, Q20]), "depth" : 2400 * mm, "offsetDistance" : 25 * mm});
        }
        {
            var Q0;
            Q0=qCreatedBy(makeId("Top.planeOp"),FACE);
            cPlane(context, id + "F3", {"entities" : qUnion([Q0]), "cplaneType" : CPlaneType.OFFSET, "offset" : 470 * mm, "width" : 150 * mm, "height" : 150 * mm});
        }
        {
            var Q0;
            Q0=qCreatedBy(makeId("Top.planeOp"),FACE);
            cPlane(context, id + "F4", {"entities" : qUnion([Q0]), "cplaneType" : CPlaneType.OFFSET, "offset" : 740 * mm, "width" : 150 * mm, "height" : 150 * mm});
        }
        {
            var Q0;
            Q0=qCreatedBy(makeId("Top.planeOp"),FACE);
            cPlane(context, id + "F5", {"entities" : qUnion([Q0]), "cplaneType" : CPlaneType.OFFSET, "offset" : 900 * mm, "width" : 150 * mm, "height" : 150 * mm});
        }
        {
            var Q0;
            Q0=qCreatedBy(makeId("Top.planeOp"),FACE);
            cPlane(context, id + "F6", {"entities" : qUnion([Q0]), "cplaneType" : CPlaneType.OFFSET, "offset" : 1200 * mm, "width" : 150 * mm, "height" : 150 * mm});
        }
        {
            var Q0;
            Q0=qCreatedBy(id+"F6.planeOp",FACE);
            var sketch = newSketch(context, id + "F7", { "sketchPlane" : qUnion([Q0])});
            skLineSegment(sketch, "E263.0.0", {"start": v(91.05, 351.97) * mm, "end": v(2364.06, 351.97) * mm});
            skLineSegment(sketch, "E263.0.1", {"start": v(2364.06, 351.97) * mm, "end": v(2391.05, 351.97) * mm});
            skLineSegment(sketch, "E263.0.2", {"start": v(2391.05, 351.97) * mm, "end": v(2391.05, 551.97) * mm});
            skLineSegment(sketch, "E263.0.3", {"start": v(2391.05, 551.97) * mm, "end": v(2364.06, 551.97) * mm});
            skLineSegment(sketch, "E263.0.4", {"start": v(2364.06, 551.97) * mm, "end": v(91.05, 551.97) * mm});
            skLineSegment(sketch, "E263.0.5", {"start": v(91.05, 551.97) * mm, "end": v(91.05, 2351.97) * mm});
            skLineSegment(sketch, "E263.0.6", {"start": v(91.05, 2351.97) * mm, "end": v(91.05, 2659.09) * mm});
            skLineSegment(sketch, "E263.0.7", {"start": v(91.05, 2659.09) * mm, "end": v(91.05, 2855) * mm});
            skLineSegment(sketch, "E263.0.8", {"start": v(91.05, 2855) * mm, "end": v(-108.95, 2855) * mm});
            skLineSegment(sketch, "E263.0.9", {"start": v(-108.95, 2855) * mm, "end": v(-108.95, 2351.97) * mm});
            skLineSegment(sketch, "E263.0.10", {"start": v(-108.95, 2351.97) * mm, "end": v(-108.95, 551.97) * mm});
            skLineSegment(sketch, "E263.0.11", {"start": v(-108.95, 551.97) * mm, "end": v(-2381.97, 551.97) * mm});
            skLineSegment(sketch, "E263.0.12", {"start": v(-2381.97, 551.97) * mm, "end": v(-2408.95, 551.97) * mm});
            skLineSegment(sketch, "E263.0.13", {"start": v(-2408.95, 551.97) * mm, "end": v(-2408.95, 351.97) * mm});
            skLineSegment(sketch, "E263.0.14", {"start": v(-2408.95, 351.97) * mm, "end": v(-2378.97, 351.97) * mm});
            skLineSegment(sketch, "E263.0.15", {"start": v(-2378.97, 351.97) * mm, "end": v(-2306.97, 351.97) * mm});
            skLineSegment(sketch, "E263.0.16", {"start": v(-2306.97, 351.97) * mm, "end": v(-108.95, 351.97) * mm});
            skLineSegment(sketch, "E263.0.17", {"start": v(-108.95, 351.97) * mm, "end": v(-108.95, -1449.23) * mm});
            skLineSegment(sketch, "E263.0.18", {"start": v(-108.95, -1449.23) * mm, "end": v(-108.95, -1945) * mm});
            skLineSegment(sketch, "E263.0.19", {"start": v(-108.95, -1945) * mm, "end": v(91.05, -1945) * mm});
            skLineSegment(sketch, "E263.0.20", {"start": v(91.05, -1945) * mm, "end": v(91.05, -1449.23) * mm});
            skLineSegment(sketch, "E263.0.21", {"start": v(91.05, -1449.23) * mm, "end": v(91.05, 351.97) * mm});
            skSolve(sketch);
        }
        {
            var Q0;
            Q0 = qSketchRegion(id + "F7", true);
            extrude(context, id + "F8", {"entities" : qUnion([Q0]), "oppositeDirection" : true, "depth" : 1200 * mm, "offsetDistance" : 25 * mm});
        }
        {
            var Q0;
            Q0=qCreatedBy(makeId("Top.planeOp"),FACE);
            var sketch = newSketch(context, id + "F9", { "sketchPlane" : qUnion([Q0])});
            skLineSegment(sketch, "E264.bottom", {"start": v(-7327.14, 6991.43) * mm, "end": v(7796.1, 6991.43) * mm});
            skLineSegment(sketch, "E264.top", {"start": v(-7327.14, -6956.14) * mm, "end": v(7796.1, -6956.14) * mm});
            skLineSegment(sketch, "E264.left", {"start": v(-7327.14, 6991.43) * mm, "end": v(-7327.14, -6956.14) * mm});
            skLineSegment(sketch, "E264.right", {"start": v(7796.1, 6991.43) * mm, "end": v(7796.1, -6956.14) * mm});
            skSolve(sketch);
        }
        {
            var Q0;
            Q0 = qSketchRegion(id + "F9", true);
            extrude(context, id + "F10", {"entities" : qUnion([Q0]), "oppositeDirection" : true, "depth" : 25 * mm, "offsetDistance" : 25 * mm});
        }
        {
            var Q0;
            Q0=qCreatedBy(id+"F3.planeOp",FACE);
            var sketch = newSketch(context, id + "F11", { "sketchPlane" : qUnion([Q0])});
            skLineSegment(sketch, "E265.0.0", {"start": v(-658.95, 2301.97) * mm, "end": v(-658.95, 1101.97) * mm});
            skLineSegment(sketch, "E265.0.1", {"start": v(-658.95, 1101.97) * mm, "end": v(-2381.97, 1101.97) * mm});
            skLineSegment(sketch, "E265.0.2", {"start": v(-2381.97, 1101.97) * mm, "end": v(-2381.97, 651.97) * mm});
            skLineSegment(sketch, "E265.0.3", {"start": v(-2381.97, 651.97) * mm, "end": v(-208.95, 651.97) * mm});
            skLineSegment(sketch, "E265.0.4", {"start": v(-208.95, 651.97) * mm, "end": v(-208.95, 2303.17) * mm});
            skLineSegment(sketch, "E265.0.5", {"start": v(-208.95, 2303.17) * mm, "end": v(-208.95, 2351.97) * mm});
            skLineSegment(sketch, "E265.0.6", {"start": v(-208.95, 2351.97) * mm, "end": v(-658.95, 2351.97) * mm});
            skLineSegment(sketch, "E265.0.7", {"start": v(-658.95, 2351.97) * mm, "end": v(-658.95, 2301.97) * mm});
            skLineSegment(sketch, "E266.0.0", {"start": v(-2378.97, 251.97) * mm, "end": v(-2378.97, -198.03) * mm});
            skLineSegment(sketch, "E266.0.1", {"start": v(-2378.97, -198.03) * mm, "end": v(-658.95, -198.03) * mm});
            skLineSegment(sketch, "E266.0.2", {"start": v(-658.95, -198.03) * mm, "end": v(-658.95, -1398.03) * mm});
            skLineSegment(sketch, "E266.0.3", {"start": v(-658.95, -1398.03) * mm, "end": v(-658.95, -1449.23) * mm});
            skLineSegment(sketch, "E266.0.4", {"start": v(-658.95, -1449.23) * mm, "end": v(-208.95, -1449.23) * mm});
            skLineSegment(sketch, "E266.0.5", {"start": v(-208.95, -1449.23) * mm, "end": v(-208.95, -1399.23) * mm});
            skLineSegment(sketch, "E266.0.6", {"start": v(-208.95, -1399.23) * mm, "end": v(-208.95, 251.97) * mm});
            skLineSegment(sketch, "E266.0.7", {"start": v(-208.95, 251.97) * mm, "end": v(-2378.97, 251.97) * mm});
            skLineSegment(sketch, "E267.0.0", {"start": v(2364.06, -198.03) * mm, "end": v(2364.06, 251.97) * mm});
            skLineSegment(sketch, "E267.0.1", {"start": v(2364.06, 251.97) * mm, "end": v(191.05, 251.97) * mm});
            skLineSegment(sketch, "E267.0.2", {"start": v(191.05, 251.97) * mm, "end": v(191.05, -1399.23) * mm});
            skLineSegment(sketch, "E267.0.3", {"start": v(191.05, -1399.23) * mm, "end": v(191.05, -1449.23) * mm});
            skLineSegment(sketch, "E267.0.4", {"start": v(191.05, -1449.23) * mm, "end": v(641.05, -1449.23) * mm});
            skLineSegment(sketch, "E267.0.5", {"start": v(641.05, -1449.23) * mm, "end": v(641.05, -1398.03) * mm});
            skLineSegment(sketch, "E267.0.6", {"start": v(641.05, -1398.03) * mm, "end": v(641.05, -198.03) * mm});
            skLineSegment(sketch, "E267.0.7", {"start": v(641.05, -198.03) * mm, "end": v(2364.06, -198.03) * mm});
            skLineSegment(sketch, "E268.0.0", {"start": v(2364.06, 1101.97) * mm, "end": v(641.05, 1101.97) * mm});
            skLineSegment(sketch, "E268.0.1", {"start": v(641.05, 1101.97) * mm, "end": v(641.05, 2301.97) * mm});
            skLineSegment(sketch, "E268.0.2", {"start": v(641.05, 2301.97) * mm, "end": v(641.05, 2351.97) * mm});
            skLineSegment(sketch, "E268.0.3", {"start": v(641.05, 2351.97) * mm, "end": v(191.05, 2351.97) * mm});
            skLineSegment(sketch, "E268.0.4", {"start": v(191.05, 2351.97) * mm, "end": v(191.05, 2303.17) * mm});
            skLineSegment(sketch, "E268.0.5", {"start": v(191.05, 2303.17) * mm, "end": v(191.05, 651.97) * mm});
            skLineSegment(sketch, "E268.0.6", {"start": v(191.05, 651.97) * mm, "end": v(2364.06, 651.97) * mm});
            skLineSegment(sketch, "E268.0.7", {"start": v(2364.06, 651.97) * mm, "end": v(2364.06, 1101.97) * mm});
            skSolve(sketch);
        }
        {
            var Q0;
            Q0 = qSketchRegion(id + "F11", true);
            extrude(context, id + "F12", {"entities" : qUnion([Q0]), "operationType" : NewBodyOperationType.ADD, "oppositeDirection" : true, "depth" : 470 * mm, "offsetDistance" : 25 * mm});
        }
        {
            var Q0;
            Q0=qCreatedBy(id+"F5.planeOp",FACE);
            var sketch = newSketch(context, id + "F13", { "sketchPlane" : qUnion([Q0])});
            skLineSegment(sketch, "E269.0.0", {"start": v(-2381.97, 651.97) * mm, "end": v(-2381.97, 551.97) * mm});
            skLineSegment(sketch, "E269.0.1", {"start": v(-2381.97, 551.97) * mm, "end": v(-108.95, 551.97) * mm});
            skLineSegment(sketch, "E269.0.2", {"start": v(-108.95, 551.97) * mm, "end": v(-108.95, 2351.97) * mm});
            skLineSegment(sketch, "E269.0.3", {"start": v(-108.95, 2351.97) * mm, "end": v(-208.95, 2351.97) * mm});
            skLineSegment(sketch, "E269.0.4", {"start": v(-208.95, 2351.97) * mm, "end": v(-208.95, 2303.17) * mm});
            skLineSegment(sketch, "E269.0.5", {"start": v(-208.95, 2303.17) * mm, "end": v(-208.95, 651.97) * mm});
            skLineSegment(sketch, "E269.0.6", {"start": v(-208.95, 651.97) * mm, "end": v(-2381.97, 651.97) * mm});
            skLineSegment(sketch, "E270.0.0", {"start": v(-208.95, -1399.23) * mm, "end": v(-208.95, -1449.23) * mm});
            skLineSegment(sketch, "E270.0.1", {"start": v(-208.95, -1449.23) * mm, "end": v(-108.95, -1449.23) * mm});
            skLineSegment(sketch, "E270.0.2", {"start": v(-108.95, -1449.23) * mm, "end": v(-108.95, 351.97) * mm});
            skLineSegment(sketch, "E270.0.3", {"start": v(-108.95, 351.97) * mm, "end": v(-2306.97, 351.97) * mm});
            skLineSegment(sketch, "E270.0.4", {"start": v(-2306.97, 351.97) * mm, "end": v(-2378.97, 351.97) * mm});
            skLineSegment(sketch, "E270.0.5", {"start": v(-2378.97, 351.97) * mm, "end": v(-2378.97, 251.97) * mm});
            skLineSegment(sketch, "E270.0.6", {"start": v(-2378.97, 251.97) * mm, "end": v(-208.95, 251.97) * mm});
            skLineSegment(sketch, "E270.0.7", {"start": v(-208.95, 251.97) * mm, "end": v(-208.95, -1399.23) * mm});
            skLineSegment(sketch, "E271.0.0", {"start": v(91.05, -1449.23) * mm, "end": v(191.05, -1449.23) * mm});
            skLineSegment(sketch, "E271.0.1", {"start": v(191.05, -1449.23) * mm, "end": v(191.05, -1399.23) * mm});
            skLineSegment(sketch, "E271.0.2", {"start": v(191.05, -1399.23) * mm, "end": v(191.05, 251.97) * mm});
            skLineSegment(sketch, "E271.0.3", {"start": v(191.05, 251.97) * mm, "end": v(2364.06, 251.97) * mm});
            skLineSegment(sketch, "E271.0.4", {"start": v(2364.06, 251.97) * mm, "end": v(2364.06, 351.97) * mm});
            skLineSegment(sketch, "E271.0.5", {"start": v(2364.06, 351.97) * mm, "end": v(91.05, 351.97) * mm});
            skLineSegment(sketch, "E271.0.6", {"start": v(91.05, 351.97) * mm, "end": v(91.05, -1449.23) * mm});
            skLineSegment(sketch, "E272.0.0", {"start": v(91.05, 551.97) * mm, "end": v(2364.06, 551.97) * mm});
            skLineSegment(sketch, "E272.0.1", {"start": v(2364.06, 551.97) * mm, "end": v(2364.06, 651.97) * mm});
            skLineSegment(sketch, "E272.0.2", {"start": v(2364.06, 651.97) * mm, "end": v(191.05, 651.97) * mm});
            skLineSegment(sketch, "E272.0.3", {"start": v(191.05, 651.97) * mm, "end": v(191.05, 2303.17) * mm});
            skLineSegment(sketch, "E272.0.4", {"start": v(191.05, 2303.17) * mm, "end": v(191.05, 2351.97) * mm});
            skLineSegment(sketch, "E272.0.5", {"start": v(191.05, 2351.97) * mm, "end": v(91.05, 2351.97) * mm});
            skLineSegment(sketch, "E272.0.6", {"start": v(91.05, 2351.97) * mm, "end": v(91.05, 551.97) * mm});
            skSolve(sketch);
        }
        {
            var Q0;
            Q0 = qSketchRegion(id + "F13", true);
            extrude(context, id + "F14", {"entities" : qUnion([Q0]), "oppositeDirection" : true, "depth" : 900 * mm, "offsetDistance" : 25 * mm});
        }
        {
            var Q0;
            Q0=qCreatedBy(id+"F4.planeOp",FACE);
            var sketch = newSketch(context, id + "F15", { "sketchPlane" : qUnion([Q0])});
            skLineSegment(sketch, "E273.0.0", {"start": v(-658.95, -198.03) * mm, "end": v(-2378.97, -198.03) * mm});
            skLineSegment(sketch, "E273.0.1", {"start": v(-2378.97, -198.03) * mm, "end": v(-2378.97, -1398.03) * mm});
            skLineSegment(sketch, "E273.0.2", {"start": v(-2378.97, -1398.03) * mm, "end": v(-658.95, -1398.03) * mm});
            skLineSegment(sketch, "E273.0.3", {"start": v(-658.95, -1398.03) * mm, "end": v(-658.95, -198.03) * mm});
            skLineSegment(sketch, "E274.0.0", {"start": v(641.05, -198.03) * mm, "end": v(641.05, -1398.03) * mm});
            skLineSegment(sketch, "E274.0.1", {"start": v(641.05, -1398.03) * mm, "end": v(2364.06, -1398.03) * mm});
            skLineSegment(sketch, "E274.0.2", {"start": v(2364.06, -1398.03) * mm, "end": v(2364.06, -198.03) * mm});
            skLineSegment(sketch, "E274.0.3", {"start": v(2364.06, -198.03) * mm, "end": v(641.05, -198.03) * mm});
            skLineSegment(sketch, "E275.0.0", {"start": v(641.05, 2301.97) * mm, "end": v(641.05, 1101.97) * mm});
            skLineSegment(sketch, "E275.0.1", {"start": v(641.05, 1101.97) * mm, "end": v(2364.06, 1101.97) * mm});
            skLineSegment(sketch, "E275.0.2", {"start": v(2364.06, 1101.97) * mm, "end": v(2364.06, 2301.97) * mm});
            skLineSegment(sketch, "E275.0.3", {"start": v(2364.06, 2301.97) * mm, "end": v(641.05, 2301.97) * mm});
            skLineSegment(sketch, "E276.0.0", {"start": v(-2381.97, 1101.97) * mm, "end": v(-658.95, 1101.97) * mm});
            skLineSegment(sketch, "E276.0.1", {"start": v(-658.95, 1101.97) * mm, "end": v(-658.95, 2301.97) * mm});
            skLineSegment(sketch, "E276.0.2", {"start": v(-658.95, 2301.97) * mm, "end": v(-2381.97, 2301.97) * mm});
            skLineSegment(sketch, "E276.0.3", {"start": v(-2381.97, 2301.97) * mm, "end": v(-2381.97, 1101.97) * mm});
            skLineSegment(sketch, "E277.0.0", {"start": v(-4690.36, 3770.67) * mm, "end": v(-5185.33, 3275.7) * mm});
            skLineSegment(sketch, "E277.0.1", {"start": v(-5185.33, 3275.7) * mm, "end": v(-4690.36, 2780.72) * mm});
            skLineSegment(sketch, "E277.0.2", {"start": v(-4690.36, 2780.72) * mm, "end": v(-4195.38, 3275.7) * mm});
            skLineSegment(sketch, "E277.0.3", {"start": v(-4195.38, 3275.7) * mm, "end": v(-4690.36, 3770.67) * mm});
            skLineSegment(sketch, "E278.0.0", {"start": v(-4152.39, 3249.78) * mm, "end": v(-4647.36, 2754.8) * mm});
            skLineSegment(sketch, "E278.0.1", {"start": v(-4647.36, 2754.8) * mm, "end": v(-4152.39, 2259.83) * mm});
            skLineSegment(sketch, "E278.0.2", {"start": v(-4152.39, 2259.83) * mm, "end": v(-3657.41, 2754.8) * mm});
            skLineSegment(sketch, "E278.0.3", {"start": v(-3657.41, 2754.8) * mm, "end": v(-4152.39, 3249.78) * mm});
            skLineSegment(sketch, "E279.0.0", {"start": v(-4474.43, 932.23) * mm, "end": v(-4474.43, 1632.23) * mm});
            skLineSegment(sketch, "E279.0.1", {"start": v(-4474.43, 1632.23) * mm, "end": v(-5174.43, 1632.23) * mm});
            skLineSegment(sketch, "E279.0.2", {"start": v(-5174.43, 1632.23) * mm, "end": v(-5174.43, 932.23) * mm});
            skLineSegment(sketch, "E279.0.3", {"start": v(-5174.43, 932.23) * mm, "end": v(-4474.43, 932.23) * mm});
            skLineSegment(sketch, "E280.0.0", {"start": v(-4474.43, 109.45) * mm, "end": v(-4474.43, 809.45) * mm});
            skLineSegment(sketch, "E280.0.1", {"start": v(-4474.43, 809.45) * mm, "end": v(-5174.43, 809.45) * mm});
            skLineSegment(sketch, "E280.0.2", {"start": v(-5174.43, 809.45) * mm, "end": v(-5174.43, 109.45) * mm});
            skLineSegment(sketch, "E280.0.3", {"start": v(-5174.43, 109.45) * mm, "end": v(-4474.43, 109.45) * mm});
            skLineSegment(sketch, "E281.0.0", {"start": v(-4474.43, -757.81) * mm, "end": v(-4474.43, -57.81) * mm});
            skLineSegment(sketch, "E281.0.1", {"start": v(-4474.43, -57.81) * mm, "end": v(-5174.43, -57.81) * mm});
            skLineSegment(sketch, "E281.0.2", {"start": v(-5174.43, -57.81) * mm, "end": v(-5174.43, -757.81) * mm});
            skLineSegment(sketch, "E281.0.3", {"start": v(-5174.43, -757.81) * mm, "end": v(-4474.43, -757.81) * mm});
            skLineSegment(sketch, "E282.0.0", {"start": v(-4690.36, -1870.72) * mm, "end": v(-5185.33, -2365.7) * mm});
            skLineSegment(sketch, "E282.0.1", {"start": v(-5185.33, -2365.7) * mm, "end": v(-4690.36, -2860.67) * mm});
            skLineSegment(sketch, "E282.0.2", {"start": v(-4690.36, -2860.67) * mm, "end": v(-4195.38, -2365.7) * mm});
            skLineSegment(sketch, "E282.0.3", {"start": v(-4195.38, -2365.7) * mm, "end": v(-4690.36, -1870.72) * mm});
            skLineSegment(sketch, "E283.0.0", {"start": v(-4152.39, -1349.83) * mm, "end": v(-4647.36, -1844.8) * mm});
            skLineSegment(sketch, "E283.0.1", {"start": v(-4647.36, -1844.8) * mm, "end": v(-4152.39, -2339.78) * mm});
            skLineSegment(sketch, "E283.0.2", {"start": v(-4152.39, -2339.78) * mm, "end": v(-3657.41, -1844.8) * mm});
            skLineSegment(sketch, "E283.0.3", {"start": v(-3657.41, -1844.8) * mm, "end": v(-4152.39, -1349.83) * mm});
            skLineSegment(sketch, "E284.0.0", {"start": v(-3218.24, -3409.56) * mm, "end": v(-3713.2, -3904.53) * mm});
            skLineSegment(sketch, "E284.0.1", {"start": v(-3713.2, -3904.53) * mm, "end": v(-3218.24, -4399.5) * mm});
            skLineSegment(sketch, "E284.0.2", {"start": v(-3218.24, -4399.5) * mm, "end": v(-2723.26, -3904.53) * mm});
            skLineSegment(sketch, "E284.0.3", {"start": v(-2723.26, -3904.53) * mm, "end": v(-3218.24, -3409.56) * mm});
            skLineSegment(sketch, "E285.0.0", {"start": v(-2680.27, -2888.67) * mm, "end": v(-3175.24, -3383.64) * mm});
            skLineSegment(sketch, "E285.0.1", {"start": v(-3175.24, -3383.64) * mm, "end": v(-2680.27, -3878.62) * mm});
            skLineSegment(sketch, "E285.0.2", {"start": v(-2680.27, -3878.62) * mm, "end": v(-2185.3, -3383.64) * mm});
            skLineSegment(sketch, "E285.0.3", {"start": v(-2185.3, -3383.64) * mm, "end": v(-2680.27, -2888.67) * mm});
            skLineSegment(sketch, "E286.0.0", {"start": v(2776.75, -4904.66) * mm, "end": v(3271.73, -4409.68) * mm});
            skLineSegment(sketch, "E286.0.1", {"start": v(3271.73, -4409.68) * mm, "end": v(2776.75, -3914.7) * mm});
            skLineSegment(sketch, "E286.0.2", {"start": v(2776.75, -3914.7) * mm, "end": v(2281.78, -4409.68) * mm});
            skLineSegment(sketch, "E286.0.3", {"start": v(2281.78, -4409.68) * mm, "end": v(2776.75, -4904.66) * mm});
            skLineSegment(sketch, "E287.0.0", {"start": v(2238.78, -4383.77) * mm, "end": v(2733.76, -3888.8) * mm});
            skLineSegment(sketch, "E287.0.1", {"start": v(2733.76, -3888.8) * mm, "end": v(2238.78, -3393.82) * mm});
            skLineSegment(sketch, "E287.0.2", {"start": v(2238.78, -3393.82) * mm, "end": v(1743.8, -3888.8) * mm});
            skLineSegment(sketch, "E287.0.3", {"start": v(1743.8, -3888.8) * mm, "end": v(2238.78, -4383.77) * mm});
            skLineSegment(sketch, "E288.0.0", {"start": v(3748.03, -90.66) * mm, "end": v(3748.03, -790.66) * mm});
            skLineSegment(sketch, "E288.0.1", {"start": v(3748.03, -790.66) * mm, "end": v(4448.03, -790.66) * mm});
            skLineSegment(sketch, "E288.0.2", {"start": v(4448.03, -790.66) * mm, "end": v(4448.03, -90.66) * mm});
            skLineSegment(sketch, "E288.0.3", {"start": v(4448.03, -90.66) * mm, "end": v(3748.03, -90.66) * mm});
            skLineSegment(sketch, "E289.0.0", {"start": v(3748.03, 1910.71) * mm, "end": v(3748.03, 1210.71) * mm});
            skLineSegment(sketch, "E289.0.1", {"start": v(3748.03, 1210.71) * mm, "end": v(4448.03, 1210.71) * mm});
            skLineSegment(sketch, "E289.0.2", {"start": v(4448.03, 1210.71) * mm, "end": v(4448.03, 1910.71) * mm});
            skLineSegment(sketch, "E289.0.3", {"start": v(4448.03, 1910.71) * mm, "end": v(3748.03, 1910.71) * mm});
            skSolve(sketch);
        }
        {
            var Q0;
            Q0 = qSketchRegion(id + "F15", true);
            extrude(context, id + "F16", {"entities" : qUnion([Q0]), "oppositeDirection" : true, "depth" : 60 * mm, "offsetDistance" : 25 * mm});
        }
        {
            var Q0;
            Q0=qCreatedBy(id+"F3.planeOp",FACE);
            var sketch = newSketch(context, id + "F17", { "sketchPlane" : qUnion([Q0])});
            skCircle(sketch, "E290.0.0", {"center": v(-4213.06, 3753) * mm, "radius": 225 * mm});
            skCircle(sketch, "E291.0.0", {"center": v(-3675.09, 3232.1) * mm, "radius": 225 * mm});
            skCircle(sketch, "E292.0.0", {"center": v(-4629.68, 2277.51) * mm, "radius": 225 * mm});
            skCircle(sketch, "E293.0", {"center": v(-5167.65, 2798.4) * mm, "radius": 225 * mm});
            skCircle(sketch, "E294.0.0", {"center": v(-5499.43, 1282.23) * mm, "radius": 225 * mm});
            skCircle(sketch, "E295.0", {"center": v(-4149.43, 1282.23) * mm, "radius": 225 * mm});
            skCircle(sketch, "E296.0.0", {"center": v(-5499.43, -407.81) * mm, "radius": 225 * mm});
            skCircle(sketch, "E297.0.0", {"center": v(-5499.43, 459.45) * mm, "radius": 225 * mm});
            skCircle(sketch, "E298.0.0", {"center": v(-4149.43, 459.45) * mm, "radius": 225 * mm});
            skCircle(sketch, "E299.0.0", {"center": v(-4149.43, -407.81) * mm, "radius": 225 * mm});
            skCircle(sketch, "E300.0.0", {"center": v(-5167.65, -1888.4) * mm, "radius": 225 * mm});
            skCircle(sketch, "E301.0.0", {"center": v(-4629.68, -1367.51) * mm, "radius": 225 * mm});
            skCircle(sketch, "E302.0.0", {"center": v(-4213.06, -2843) * mm, "radius": 225 * mm});
            skCircle(sketch, "E303.0.0", {"center": v(-3675.09, -2322.1) * mm, "radius": 225 * mm});
            skCircle(sketch, "E304.0.0", {"center": v(-2740.94, -4381.83) * mm, "radius": 225 * mm});
            skCircle(sketch, "E305.0.0", {"center": v(-2202.97, -3860.94) * mm, "radius": 225 * mm});
            skCircle(sketch, "E306.0.0", {"center": v(-3157.56, -2906.34) * mm, "radius": 225 * mm});
            skCircle(sketch, "E307.0.0", {"center": v(-3695.53, -3427.23) * mm, "radius": 225 * mm});
            skCircle(sketch, "E308.0.0", {"center": v(2299.45, -4886.98) * mm, "radius": 225 * mm});
            skCircle(sketch, "E309.0.0", {"center": v(1761.49, -4366.09) * mm, "radius": 225 * mm});
            skCircle(sketch, "E310.0.0", {"center": v(2716.08, -3411.5) * mm, "radius": 225 * mm});
            skCircle(sketch, "E311.0.0", {"center": v(3254.05, -3932.39) * mm, "radius": 225 * mm});
            skCircle(sketch, "E312.0.0", {"center": v(941.05, -1749.5) * mm, "radius": 225 * mm});
            skCircle(sketch, "E313.0.0", {"center": v(1541.05, -1749.5) * mm, "radius": 225 * mm});
            skCircle(sketch, "E314.0.0", {"center": v(2119.43, -1749.5) * mm, "radius": 225 * mm});
            skCircle(sketch, "E315.0.0", {"center": v(2681.11, -498.03) * mm, "radius": 225 * mm});
            skCircle(sketch, "E316.0.0", {"center": v(2681.11, -1098.03) * mm, "radius": 225 * mm});
            skCircle(sketch, "E317.0.0", {"center": v(2681.11, 1401.97) * mm, "radius": 225 * mm});
            skCircle(sketch, "E318.0.0", {"center": v(2681.11, 2001.97) * mm, "radius": 225 * mm});
            skCircle(sketch, "E319.0.0", {"center": v(2119.43, 2653.44) * mm, "radius": 225 * mm});
            skCircle(sketch, "E320.0.0", {"center": v(1541.05, 2653.44) * mm, "radius": 225 * mm});
            skCircle(sketch, "E321.0.0", {"center": v(941.05, 2653.44) * mm, "radius": 225 * mm});
            skCircle(sketch, "E322.0.0", {"center": v(-958.95, 2653.44) * mm, "radius": 225 * mm});
            skCircle(sketch, "E323.0", {"center": v(-1558.95, 2653.44) * mm, "radius": 225 * mm});
            skCircle(sketch, "E324.0.0", {"center": v(-2158.94, 2653.14) * mm, "radius": 225 * mm});
            skCircle(sketch, "E325.0.0", {"center": v(-2699.02, 2001.97) * mm, "radius": 225 * mm});
            skCircle(sketch, "E326.0.0", {"center": v(-2699.02, 1401.97) * mm, "radius": 225 * mm});
            skCircle(sketch, "E327.0.0", {"center": v(-2699.02, -498.03) * mm, "radius": 225 * mm});
            skCircle(sketch, "E328.0.0", {"center": v(-2699.02, -1098.03) * mm, "radius": 225 * mm});
            skCircle(sketch, "E329.0.0", {"center": v(-2137.34, -1749.5) * mm, "radius": 225 * mm});
            skCircle(sketch, "E330.0.0", {"center": v(-1558.95, -1749.5) * mm, "radius": 225 * mm});
            skCircle(sketch, "E331.0.0", {"center": v(-958.95, -1749.5) * mm, "radius": 225 * mm});
            skCircle(sketch, "E332.0.0", {"center": v(4098.03, -1115.66) * mm, "radius": 225 * mm});
            skCircle(sketch, "E333.0.0", {"center": v(4098.03, 234.34) * mm, "radius": 225 * mm});
            skCircle(sketch, "E334.0.0", {"center": v(4098.03, 885.71) * mm, "radius": 225 * mm});
            skCircle(sketch, "E335.0.0", {"center": v(4098.03, 2235.71) * mm, "radius": 225 * mm});
            skSolve(sketch);
        }
        {
            var Q0;
            Q0 = qSketchRegion(id + "F17", true);
            extrude(context, id + "F18", {"entities" : qUnion([Q0]), "oppositeDirection" : true, "depth" : 50 * mm, "offsetDistance" : 25 * mm});
        }
        {
            var Q0;
            Q0=makeQuery(id+"F2.opExtrude","CAP_FACE",FACE,{"disambiguationData":[OSD([sQuery(id+"F0.wireOp",EDGE,"E3"),sQuery(id+"F0.wireOp",EDGE,"E4"),sQuery(id+"F0.wireOp",EDGE,"E5"),sQuery(id+"F0.wireOp",EDGE,"E9"),sQuery(id+"F0.wireOp",EDGE,"E10"),sQuery(id+"F0.wireOp",EDGE,"E11"),sQuery(id+"F0.wireOp",EDGE,"E12"),sQuery(id+"F0.wireOp",EDGE,"E23"),sQuery(id+"F0.wireOp",EDGE,"E54"),sQuery(id+"F0.wireOp",EDGE,"E67")])],"isStart":false});
            var sketch = newSketch(context, id + "F19", { "sketchPlane" : qUnion([Q0])});
            skLineSegment(sketch, "E336.0.0", {"start": v(-3001.67, 5719.4) * mm, "end": v(-3079.45, 5797.2) * mm});
            skLineSegment(sketch, "E336.0.1", {"start": v(-3079.45, 5797.2) * mm, "end": v(-3645.14, 5231.5) * mm});
            skLineSegment(sketch, "E336.0.2", {"start": v(-3645.14, 5231.5) * mm, "end": v(-3567.35, 5153.72) * mm});
            skLineSegment(sketch, "E336.0.3", {"start": v(-3567.35, 5153.72) * mm, "end": v(-3001.67, 5719.4) * mm});
            skLineSegment(sketch, "E337.0.0", {"start": v(-3991.62, 4729.46) * mm, "end": v(-4069.4, 4807.24) * mm});
            skLineSegment(sketch, "E337.0.1", {"start": v(-4069.4, 4807.24) * mm, "end": v(-4635.08, 4241.56) * mm});
            skLineSegment(sketch, "E337.0.2", {"start": v(-4635.08, 4241.56) * mm, "end": v(-4557.3, 4163.78) * mm});
            skLineSegment(sketch, "E337.0.3", {"start": v(-4557.3, 4163.78) * mm, "end": v(-3991.62, 4729.46) * mm});
            skLineSegment(sketch, "E338.0.0", {"start": v(-4981.57, 3739.51) * mm, "end": v(-5059.35, 3817.3) * mm});
            skLineSegment(sketch, "E338.0.1", {"start": v(-5059.35, 3817.3) * mm, "end": v(-5625.03, 3251.6) * mm});
            skLineSegment(sketch, "E338.0.2", {"start": v(-5625.03, 3251.6) * mm, "end": v(-5547.25, 3173.83) * mm});
            skLineSegment(sketch, "E338.0.3", {"start": v(-5547.25, 3173.83) * mm, "end": v(-4981.57, 3739.51) * mm});
            skLineSegment(sketch, "E339.0.0", {"start": v(-5955, 1455) * mm, "end": v(-5845, 1455) * mm});
            skLineSegment(sketch, "E339.0.1", {"start": v(-5845, 1455) * mm, "end": v(-5845, 2255) * mm});
            skLineSegment(sketch, "E339.0.2", {"start": v(-5845, 2255) * mm, "end": v(-5955, 2255) * mm});
            skLineSegment(sketch, "E339.0.3", {"start": v(-5955, 2255) * mm, "end": v(-5955, 1855) * mm});
            skLineSegment(sketch, "E339.0.4", {"start": v(-5955, 1855) * mm, "end": v(-5955, 1455) * mm});
            skLineSegment(sketch, "E340.0.0", {"start": v(-5845, 55) * mm, "end": v(-5845, 855) * mm});
            skLineSegment(sketch, "E340.0.1", {"start": v(-5845, 855) * mm, "end": v(-5955, 855) * mm});
            skLineSegment(sketch, "E340.0.2", {"start": v(-5955, 855) * mm, "end": v(-5955, 55) * mm});
            skLineSegment(sketch, "E340.0.3", {"start": v(-5955, 55) * mm, "end": v(-5845, 55) * mm});
            skLineSegment(sketch, "E341.0.0", {"start": v(-5955, -1345) * mm, "end": v(-5845, -1345) * mm});
            skLineSegment(sketch, "E341.0.1", {"start": v(-5845, -1345) * mm, "end": v(-5845, -545) * mm});
            skLineSegment(sketch, "E341.0.2", {"start": v(-5845, -545) * mm, "end": v(-5955, -545) * mm});
            skLineSegment(sketch, "E341.0.3", {"start": v(-5955, -545) * mm, "end": v(-5955, -945) * mm});
            skLineSegment(sketch, "E341.0.4", {"start": v(-5955, -945) * mm, "end": v(-5955, -1345) * mm});
            skLineSegment(sketch, "E342.0.0", {"start": v(-5547.25, -2263.83) * mm, "end": v(-5625.03, -2341.6) * mm});
            skLineSegment(sketch, "E342.0.1", {"start": v(-5625.03, -2341.6) * mm, "end": v(-5059.35, -2907.3) * mm});
            skLineSegment(sketch, "E342.0.2", {"start": v(-5059.35, -2907.3) * mm, "end": v(-4981.57, -2829.51) * mm});
            skLineSegment(sketch, "E342.0.3", {"start": v(-4981.57, -2829.51) * mm, "end": v(-5547.25, -2263.83) * mm});
            skLineSegment(sketch, "E343.0", {"start": v(-5845, -1966.08) * mm, "end": v(-2421.08, -5390) * mm});
            skLineSegment(sketch, "E344.0.0", {"start": v(-1445, -3495) * mm, "end": v(1445, -3495) * mm, "construction": true});
            skLineSegment(sketch, "E344.0.1", {"start": v(1445, -3495) * mm, "end": v(1445, -5390) * mm, "construction": true});
            skLineSegment(sketch, "E344.0.2", {"start": v(1445, -5390) * mm, "end": v(2020, -5390) * mm});
            skLineSegment(sketch, "E344.0.3", {"start": v(2020, -5390) * mm, "end": v(2421.08, -5390) * mm});
            skLineSegment(sketch, "E344.0.4", {"start": v(2421.08, -5390) * mm, "end": v(3001.67, -4809.4) * mm});
            skLineSegment(sketch, "E344.0.5", {"start": v(3001.67, -4809.4) * mm, "end": v(3567.35, -4243.72) * mm});
            skLineSegment(sketch, "E344.0.6", {"start": v(3567.35, -4243.72) * mm, "end": v(3991.62, -3819.46) * mm});
            skLineSegment(sketch, "E344.0.7", {"start": v(3991.62, -3819.46) * mm, "end": v(4557.3, -3253.78) * mm});
            skLineSegment(sketch, "E344.0.8", {"start": v(4557.3, -3253.78) * mm, "end": v(4981.57, -2829.51) * mm});
            skLineSegment(sketch, "E344.0.9", {"start": v(4981.57, -2829.51) * mm, "end": v(5322.82, -2488.26) * mm});
            skLineSegment(sketch, "E344.0.10", {"start": v(5322.82, -2488.26) * mm, "end": v(4403.58, -1569.02) * mm, "construction": true});
            skLineSegment(sketch, "E344.0.11", {"start": v(4403.58, -1569.02) * mm, "end": v(4545, -1427.6) * mm, "construction": true});
            skLineSegment(sketch, "E344.0.12", {"start": v(4545, -1427.6) * mm, "end": v(4545, 2337.6) * mm, "construction": true});
            skLineSegment(sketch, "E344.0.13", {"start": v(4545, 2337.6) * mm, "end": v(3837.9, 3044.7) * mm, "construction": true});
            skLineSegment(sketch, "E344.0.14", {"start": v(3837.9, 3044.7) * mm, "end": v(4757.13, 3963.95) * mm, "construction": true});
            skLineSegment(sketch, "E344.0.15", {"start": v(4757.13, 3963.95) * mm, "end": v(2421.08, 6300) * mm});
            skLineSegment(sketch, "E344.0.16", {"start": v(2421.08, 6300) * mm, "end": v(0, 6300) * mm});
            skLineSegment(sketch, "E344.0.17", {"start": v(0, 6300) * mm, "end": v(-2421.08, 6300) * mm});
            skLineSegment(sketch, "E344.0.18", {"start": v(-2421.08, 6300) * mm, "end": v(-3001.67, 5719.4) * mm});
            skLineSegment(sketch, "E344.0.19", {"start": v(-3001.67, 5719.4) * mm, "end": v(-3567.35, 5153.72) * mm});
            skLineSegment(sketch, "E344.0.20", {"start": v(-3567.35, 5153.72) * mm, "end": v(-3991.62, 4729.46) * mm});
            skLineSegment(sketch, "E344.0.21", {"start": v(-3991.62, 4729.46) * mm, "end": v(-4557.3, 4163.78) * mm});
            skLineSegment(sketch, "E344.0.22", {"start": v(-4557.3, 4163.78) * mm, "end": v(-4981.57, 3739.51) * mm});
            skLineSegment(sketch, "E344.0.23", {"start": v(-4981.57, 3739.51) * mm, "end": v(-5547.25, 3173.83) * mm});
            skLineSegment(sketch, "E344.0.24", {"start": v(-5547.25, 3173.83) * mm, "end": v(-5845, 2876.08) * mm});
            skLineSegment(sketch, "E344.0.25", {"start": v(-5845, 2876.08) * mm, "end": v(-5845, 2255) * mm});
            skLineSegment(sketch, "E344.0.26", {"start": v(-5845, 2255) * mm, "end": v(-5845, 1455) * mm});
            skLineSegment(sketch, "E344.0.27", {"start": v(-5845, 1455) * mm, "end": v(-5845, 855) * mm});
            skLineSegment(sketch, "E344.0.28", {"start": v(-5845, 855) * mm, "end": v(-5845, 55) * mm});
            skLineSegment(sketch, "E344.0.29", {"start": v(-5845, 55) * mm, "end": v(-5845, -545) * mm});
            skLineSegment(sketch, "E344.0.30", {"start": v(-5845, -545) * mm, "end": v(-5845, -1345) * mm});
            skLineSegment(sketch, "E344.0.31", {"start": v(-5845, -1345) * mm, "end": v(-5845, -1966.08) * mm});
            skLineSegment(sketch, "E344.0.32", {"start": v(-5845, -1966.08) * mm, "end": v(-5547.25, -2263.83) * mm});
            skLineSegment(sketch, "E344.0.33", {"start": v(-5547.25, -2263.83) * mm, "end": v(-4981.57, -2829.51) * mm});
            skLineSegment(sketch, "E344.0.34", {"start": v(-4981.57, -2829.51) * mm, "end": v(-4557.3, -3253.78) * mm});
            skLineSegment(sketch, "E344.0.35", {"start": v(-4557.3, -3253.78) * mm, "end": v(-3991.62, -3819.46) * mm});
            skLineSegment(sketch, "E344.0.36", {"start": v(-3991.62, -3819.46) * mm, "end": v(-3567.35, -4243.72) * mm});
            skLineSegment(sketch, "E344.0.37", {"start": v(-3567.35, -4243.72) * mm, "end": v(-3001.67, -4809.4) * mm});
            skLineSegment(sketch, "E344.0.38", {"start": v(-3001.67, -4809.4) * mm, "end": v(-2421.08, -5390) * mm});
            skLineSegment(sketch, "E344.0.39", {"start": v(-2421.08, -5390) * mm, "end": v(-2020, -5390) * mm});
            skLineSegment(sketch, "E344.0.40", {"start": v(-2020, -5390) * mm, "end": v(-1445, -5390) * mm});
            skLineSegment(sketch, "E344.0.41", {"start": v(-1445, -5390) * mm, "end": v(-1445, -3495) * mm, "construction": true});
            skLineSegment(sketch, "E345.0.0", {"start": v(-4557.3, -3253.78) * mm, "end": v(-4635.08, -3331.56) * mm});
            skLineSegment(sketch, "E345.0.1", {"start": v(-4635.08, -3331.56) * mm, "end": v(-4069.4, -3897.24) * mm});
            skLineSegment(sketch, "E345.0.2", {"start": v(-4069.4, -3897.24) * mm, "end": v(-3991.62, -3819.46) * mm});
            skLineSegment(sketch, "E345.0.3", {"start": v(-3991.62, -3819.46) * mm, "end": v(-4557.3, -3253.78) * mm});
            skLineSegment(sketch, "E346.0.0", {"start": v(-3645.14, -4321.5) * mm, "end": v(-3079.45, -4887.2) * mm});
            skLineSegment(sketch, "E346.0.1", {"start": v(-3079.45, -4887.2) * mm, "end": v(-3001.67, -4809.4) * mm});
            skLineSegment(sketch, "E346.0.2", {"start": v(-3001.67, -4809.4) * mm, "end": v(-3567.35, -4243.72) * mm});
            skLineSegment(sketch, "E346.0.3", {"start": v(-3567.35, -4243.72) * mm, "end": v(-3645.14, -4321.5) * mm});
            skLineSegment(sketch, "E347.0.0", {"start": v(-1445, -5390) * mm, "end": v(-2020, -5390) * mm});
            skLineSegment(sketch, "E347.0.1", {"start": v(-2020, -5390) * mm, "end": v(-2020, -5500) * mm});
            skLineSegment(sketch, "E347.0.2", {"start": v(-2020, -5500) * mm, "end": v(-1120, -5500) * mm});
            skLineSegment(sketch, "E347.0.3", {"start": v(-1120, -5500) * mm, "end": v(-1120, -5390) * mm});
            skLineSegment(sketch, "E347.0.4", {"start": v(-1120, -5390) * mm, "end": v(-1375, -5390) * mm});
            skLineSegment(sketch, "E347.0.5", {"start": v(-1375, -5390) * mm, "end": v(-1445, -5390) * mm});
            skLineSegment(sketch, "E348.0.0", {"start": v(1375, -5390) * mm, "end": v(1120, -5390) * mm});
            skLineSegment(sketch, "E348.0.1", {"start": v(1120, -5390) * mm, "end": v(1120, -5500) * mm});
            skLineSegment(sketch, "E348.0.2", {"start": v(1120, -5500) * mm, "end": v(2020, -5500) * mm});
            skLineSegment(sketch, "E348.0.3", {"start": v(2020, -5500) * mm, "end": v(2020, -5390) * mm});
            skLineSegment(sketch, "E348.0.4", {"start": v(2020, -5390) * mm, "end": v(1445, -5390) * mm});
            skLineSegment(sketch, "E348.0.5", {"start": v(1445, -5390) * mm, "end": v(1375, -5390) * mm});
            skLineSegment(sketch, "E349.0.0", {"start": v(3567.35, -4243.72) * mm, "end": v(3001.67, -4809.4) * mm});
            skLineSegment(sketch, "E349.0.1", {"start": v(3001.67, -4809.4) * mm, "end": v(3079.45, -4887.2) * mm});
            skLineSegment(sketch, "E349.0.2", {"start": v(3079.45, -4887.2) * mm, "end": v(3645.14, -4321.5) * mm});
            skLineSegment(sketch, "E349.0.3", {"start": v(3645.14, -4321.5) * mm, "end": v(3567.35, -4243.72) * mm});
            skLineSegment(sketch, "E350.0.0", {"start": v(4557.3, -3253.78) * mm, "end": v(3991.62, -3819.46) * mm});
            skLineSegment(sketch, "E350.0.1", {"start": v(3991.62, -3819.46) * mm, "end": v(4069.4, -3897.24) * mm});
            skLineSegment(sketch, "E350.0.2", {"start": v(4069.4, -3897.24) * mm, "end": v(4635.08, -3331.56) * mm});
            skLineSegment(sketch, "E350.0.3", {"start": v(4635.08, -3331.56) * mm, "end": v(4557.3, -3253.78) * mm});
            skLineSegment(sketch, "E351.0.0", {"start": v(5322.82, -2488.26) * mm, "end": v(4981.57, -2829.51) * mm});
            skLineSegment(sketch, "E351.0.1", {"start": v(4981.57, -2829.51) * mm, "end": v(5059.35, -2907.3) * mm});
            skLineSegment(sketch, "E351.0.2", {"start": v(5059.35, -2907.3) * mm, "end": v(5625.03, -2341.6) * mm});
            skLineSegment(sketch, "E351.0.3", {"start": v(5625.03, -2341.6) * mm, "end": v(5547.25, -2263.83) * mm});
            skLineSegment(sketch, "E351.0.4", {"start": v(5547.25, -2263.83) * mm, "end": v(5322.82, -2488.26) * mm});
            skLineSegment(sketch, "E352.0.0", {"start": v(5845, -545) * mm, "end": v(5845, -1345) * mm});
            skLineSegment(sketch, "E352.0.1", {"start": v(5845, -1345) * mm, "end": v(5955, -1345) * mm});
            skLineSegment(sketch, "E352.0.2", {"start": v(5955, -1345) * mm, "end": v(5955, -545) * mm});
            skLineSegment(sketch, "E352.0.3", {"start": v(5955, -545) * mm, "end": v(5845, -545) * mm});
            skLineSegment(sketch, "E353.0.0", {"start": v(5845, 855) * mm, "end": v(5845, 55) * mm});
            skLineSegment(sketch, "E353.0.1", {"start": v(5845, 55) * mm, "end": v(5955, 55) * mm});
            skLineSegment(sketch, "E353.0.2", {"start": v(5955, 55) * mm, "end": v(5955, 855) * mm});
            skLineSegment(sketch, "E353.0.3", {"start": v(5955, 855) * mm, "end": v(5845, 855) * mm});
            skLineSegment(sketch, "E354.0.0", {"start": v(5845, 2255) * mm, "end": v(5845, 1455) * mm});
            skLineSegment(sketch, "E354.0.1", {"start": v(5845, 1455) * mm, "end": v(5955, 1455) * mm});
            skLineSegment(sketch, "E354.0.2", {"start": v(5955, 1455) * mm, "end": v(5955, 2255) * mm});
            skLineSegment(sketch, "E354.0.3", {"start": v(5955, 2255) * mm, "end": v(5845, 2255) * mm});
            skSolve(sketch);
        }
        {
            var Q0;
            Q0 = qSketchRegion(id + "F19", true);
            extrude(context, id + "F20", {"entities" : qUnion([Q0]), "operationType" : NewBodyOperationType.ADD, "oppositeDirection" : true, "depth" : 600 * mm, "offsetDistance" : 25 * mm});
        }
        {
            var Q0;
            Q0=qCreatedBy(makeId("Top.planeOp"),FACE);
            var sketch = newSketch(context, id + "F21", { "sketchPlane" : qUnion([Q0])});
            skLineSegment(sketch, "E355.0.0", {"start": v(-3001.67, 5719.4) * mm, "end": v(-3079.45, 5797.2) * mm});
            skLineSegment(sketch, "E355.0.1", {"start": v(-3079.45, 5797.2) * mm, "end": v(-3645.14, 5231.5) * mm});
            skLineSegment(sketch, "E355.0.2", {"start": v(-3645.14, 5231.5) * mm, "end": v(-3567.35, 5153.72) * mm});
            skLineSegment(sketch, "E355.0.3", {"start": v(-3567.35, 5153.72) * mm, "end": v(-3001.67, 5719.4) * mm});
            skLineSegment(sketch, "E356.0.0", {"start": v(-3991.62, 4729.46) * mm, "end": v(-4069.4, 4807.24) * mm});
            skLineSegment(sketch, "E356.0.1", {"start": v(-4069.4, 4807.24) * mm, "end": v(-4635.08, 4241.56) * mm});
            skLineSegment(sketch, "E356.0.2", {"start": v(-4635.08, 4241.56) * mm, "end": v(-4557.3, 4163.78) * mm});
            skLineSegment(sketch, "E356.0.3", {"start": v(-4557.3, 4163.78) * mm, "end": v(-3991.62, 4729.46) * mm});
            skLineSegment(sketch, "E357.0.0", {"start": v(-4981.57, 3739.51) * mm, "end": v(-5059.35, 3817.3) * mm});
            skLineSegment(sketch, "E357.0.1", {"start": v(-5059.35, 3817.3) * mm, "end": v(-5625.03, 3251.6) * mm});
            skLineSegment(sketch, "E357.0.2", {"start": v(-5625.03, 3251.6) * mm, "end": v(-5547.25, 3173.83) * mm});
            skLineSegment(sketch, "E357.0.3", {"start": v(-5547.25, 3173.83) * mm, "end": v(-4981.57, 3739.51) * mm});
            skLineSegment(sketch, "E358.0.0", {"start": v(-5955, 1455) * mm, "end": v(-5845, 1455) * mm});
            skLineSegment(sketch, "E358.0.1", {"start": v(-5845, 1455) * mm, "end": v(-5845, 2255) * mm});
            skLineSegment(sketch, "E358.0.2", {"start": v(-5845, 2255) * mm, "end": v(-5955, 2255) * mm});
            skLineSegment(sketch, "E358.0.3", {"start": v(-5955, 2255) * mm, "end": v(-5955, 1855) * mm});
            skLineSegment(sketch, "E358.0.4", {"start": v(-5955, 1855) * mm, "end": v(-5955, 1455) * mm});
            skLineSegment(sketch, "E359.0.0", {"start": v(-5845, 55) * mm, "end": v(-5845, 855) * mm});
            skLineSegment(sketch, "E359.0.1", {"start": v(-5845, 855) * mm, "end": v(-5955, 855) * mm});
            skLineSegment(sketch, "E359.0.2", {"start": v(-5955, 855) * mm, "end": v(-5955, 55) * mm});
            skLineSegment(sketch, "E359.0.3", {"start": v(-5955, 55) * mm, "end": v(-5845, 55) * mm});
            skLineSegment(sketch, "E360.0.0", {"start": v(-5955, -1345) * mm, "end": v(-5845, -1345) * mm});
            skLineSegment(sketch, "E360.0.1", {"start": v(-5845, -1345) * mm, "end": v(-5845, -545) * mm});
            skLineSegment(sketch, "E360.0.2", {"start": v(-5845, -545) * mm, "end": v(-5955, -545) * mm});
            skLineSegment(sketch, "E360.0.3", {"start": v(-5955, -545) * mm, "end": v(-5955, -945) * mm});
            skLineSegment(sketch, "E360.0.4", {"start": v(-5955, -945) * mm, "end": v(-5955, -1345) * mm});
            skLineSegment(sketch, "E361.0.0", {"start": v(-5547.25, -2263.83) * mm, "end": v(-5625.03, -2341.6) * mm});
            skLineSegment(sketch, "E361.0.1", {"start": v(-5625.03, -2341.6) * mm, "end": v(-5059.35, -2907.3) * mm});
            skLineSegment(sketch, "E361.0.2", {"start": v(-5059.35, -2907.3) * mm, "end": v(-4981.57, -2829.51) * mm});
            skLineSegment(sketch, "E361.0.3", {"start": v(-4981.57, -2829.51) * mm, "end": v(-5547.25, -2263.83) * mm});
            skLineSegment(sketch, "E362.0.0", {"start": v(-4557.3, -3253.78) * mm, "end": v(-4635.08, -3331.56) * mm});
            skLineSegment(sketch, "E362.0.1", {"start": v(-4635.08, -3331.56) * mm, "end": v(-4069.4, -3897.24) * mm});
            skLineSegment(sketch, "E362.0.2", {"start": v(-4069.4, -3897.24) * mm, "end": v(-3991.62, -3819.46) * mm});
            skLineSegment(sketch, "E362.0.3", {"start": v(-3991.62, -3819.46) * mm, "end": v(-4557.3, -3253.78) * mm});
            skLineSegment(sketch, "E363.0.0", {"start": v(-3645.14, -4321.5) * mm, "end": v(-3079.45, -4887.2) * mm});
            skLineSegment(sketch, "E363.0.1", {"start": v(-3079.45, -4887.2) * mm, "end": v(-3001.67, -4809.4) * mm});
            skLineSegment(sketch, "E363.0.2", {"start": v(-3001.67, -4809.4) * mm, "end": v(-3567.35, -4243.72) * mm});
            skLineSegment(sketch, "E363.0.3", {"start": v(-3567.35, -4243.72) * mm, "end": v(-3645.14, -4321.5) * mm});
            skLineSegment(sketch, "E364.0.0", {"start": v(-1445, -5390) * mm, "end": v(-2020, -5390) * mm});
            skLineSegment(sketch, "E364.0.1", {"start": v(-2020, -5390) * mm, "end": v(-2020, -5500) * mm});
            skLineSegment(sketch, "E364.0.2", {"start": v(-2020, -5500) * mm, "end": v(-1120, -5500) * mm});
            skLineSegment(sketch, "E364.0.3", {"start": v(-1120, -5500) * mm, "end": v(-1120, -5390) * mm});
            skLineSegment(sketch, "E364.0.4", {"start": v(-1120, -5390) * mm, "end": v(-1375, -5390) * mm});
            skLineSegment(sketch, "E364.0.5", {"start": v(-1375, -5390) * mm, "end": v(-1445, -5390) * mm});
            skLineSegment(sketch, "E365.0.0", {"start": v(1375, -5390) * mm, "end": v(1120, -5390) * mm});
            skLineSegment(sketch, "E365.0.1", {"start": v(1120, -5390) * mm, "end": v(1120, -5500) * mm});
            skLineSegment(sketch, "E365.0.2", {"start": v(1120, -5500) * mm, "end": v(2020, -5500) * mm});
            skLineSegment(sketch, "E365.0.3", {"start": v(2020, -5500) * mm, "end": v(2020, -5390) * mm});
            skLineSegment(sketch, "E365.0.4", {"start": v(2020, -5390) * mm, "end": v(1445, -5390) * mm});
            skLineSegment(sketch, "E365.0.5", {"start": v(1445, -5390) * mm, "end": v(1375, -5390) * mm});
            skLineSegment(sketch, "E366.0.0", {"start": v(3567.35, -4243.72) * mm, "end": v(3001.67, -4809.4) * mm});
            skLineSegment(sketch, "E366.0.1", {"start": v(3001.67, -4809.4) * mm, "end": v(3079.45, -4887.2) * mm});
            skLineSegment(sketch, "E366.0.2", {"start": v(3079.45, -4887.2) * mm, "end": v(3645.14, -4321.5) * mm});
            skLineSegment(sketch, "E366.0.3", {"start": v(3645.14, -4321.5) * mm, "end": v(3567.35, -4243.72) * mm});
            skLineSegment(sketch, "E367.0.0", {"start": v(4557.3, -3253.78) * mm, "end": v(3991.62, -3819.46) * mm});
            skLineSegment(sketch, "E367.0.1", {"start": v(3991.62, -3819.46) * mm, "end": v(4069.4, -3897.24) * mm});
            skLineSegment(sketch, "E367.0.2", {"start": v(4069.4, -3897.24) * mm, "end": v(4635.08, -3331.56) * mm});
            skLineSegment(sketch, "E367.0.3", {"start": v(4635.08, -3331.56) * mm, "end": v(4557.3, -3253.78) * mm});
            skLineSegment(sketch, "E368.0.0", {"start": v(5322.82, -2488.26) * mm, "end": v(4981.57, -2829.51) * mm});
            skLineSegment(sketch, "E368.0.1", {"start": v(4981.57, -2829.51) * mm, "end": v(5059.35, -2907.3) * mm});
            skLineSegment(sketch, "E368.0.2", {"start": v(5059.35, -2907.3) * mm, "end": v(5625.03, -2341.6) * mm});
            skLineSegment(sketch, "E368.0.3", {"start": v(5625.03, -2341.6) * mm, "end": v(5547.25, -2263.83) * mm});
            skLineSegment(sketch, "E368.0.4", {"start": v(5547.25, -2263.83) * mm, "end": v(5322.82, -2488.26) * mm});
            skLineSegment(sketch, "E369.0.0", {"start": v(5845, -545) * mm, "end": v(5845, -1345) * mm});
            skLineSegment(sketch, "E369.0.1", {"start": v(5845, -1345) * mm, "end": v(5955, -1345) * mm});
            skLineSegment(sketch, "E369.0.2", {"start": v(5955, -1345) * mm, "end": v(5955, -545) * mm});
            skLineSegment(sketch, "E369.0.3", {"start": v(5955, -545) * mm, "end": v(5845, -545) * mm});
            skLineSegment(sketch, "E370.0.0", {"start": v(5845, 855) * mm, "end": v(5845, 55) * mm});
            skLineSegment(sketch, "E370.0.1", {"start": v(5845, 55) * mm, "end": v(5955, 55) * mm});
            skLineSegment(sketch, "E370.0.2", {"start": v(5955, 55) * mm, "end": v(5955, 855) * mm});
            skLineSegment(sketch, "E370.0.3", {"start": v(5955, 855) * mm, "end": v(5845, 855) * mm});
            skLineSegment(sketch, "E371.0.0", {"start": v(5845, 2255) * mm, "end": v(5845, 1455) * mm});
            skLineSegment(sketch, "E371.0.1", {"start": v(5845, 1455) * mm, "end": v(5955, 1455) * mm});
            skLineSegment(sketch, "E371.0.2", {"start": v(5955, 1455) * mm, "end": v(5955, 2255) * mm});
            skLineSegment(sketch, "E371.0.3", {"start": v(5955, 2255) * mm, "end": v(5845, 2255) * mm});
            skSolve(sketch);
        }
        {
            var Q0;
            Q0 = qSketchRegion(id + "F21", true);
            extrude(context, id + "F22", {"entities" : qUnion([Q0]), "operationType" : NewBodyOperationType.ADD, "depth" : 1100 * mm, "offsetDistance" : 25 * mm});
        }
        {
            var Q0;
            Q0=makeQuery(id+"F10.opExtrude","CAP_FACE",FACE,{"disambiguationData":[OSD([sQuery(id+"F9.wireOp",EDGE,"E264.bottom"),sQuery(id+"F9.wireOp",EDGE,"E264.top"),sQuery(id+"F9.wireOp",EDGE,"E264.left"),sQuery(id+"F9.wireOp",EDGE,"E264.right")])],"isStart":true});
            var sketch = newSketch(context, id + "F23", { "sketchPlane" : qUnion([Q0])});
            skCircle(sketch, "E372", {"center": v(-2740.94, -4381.83) * mm, "radius": 40 * mm});
            skCircle(sketch, "E373", {"center": v(-2202.97, -3860.94) * mm, "radius": 40 * mm});
            skCircle(sketch, "E374", {"center": v(-3695.53, -3427.23) * mm, "radius": 40 * mm});
            skCircle(sketch, "E375", {"center": v(-3157.56, -2906.34) * mm, "radius": 40 * mm});
            skCircle(sketch, "E376", {"center": v(-4213.06, -2843) * mm, "radius": 40 * mm});
            skCircle(sketch, "E377", {"center": v(-3675.09, -2322.1) * mm, "radius": 40 * mm});
            skCircle(sketch, "E378", {"center": v(-5167.65, -1888.4) * mm, "radius": 40 * mm});
            skCircle(sketch, "E379", {"center": v(-4629.68, -1367.51) * mm, "radius": 40 * mm});
            skCircle(sketch, "E380", {"center": v(-5499.43, -407.81) * mm, "radius": 40 * mm});
            skCircle(sketch, "E381", {"center": v(-4149.43, -407.81) * mm, "radius": 40 * mm});
            skCircle(sketch, "E382", {"center": v(-5499.43, 459.45) * mm, "radius": 40 * mm});
            skCircle(sketch, "E383", {"center": v(-4149.43, 459.45) * mm, "radius": 40 * mm});
            skCircle(sketch, "E384", {"center": v(-4149.43, 1282.23) * mm, "radius": 40 * mm});
            skCircle(sketch, "E385", {"center": v(-5499.43, 1282.23) * mm, "radius": 40 * mm});
            skCircle(sketch, "E386", {"center": v(-4629.68, 2277.51) * mm, "radius": 40 * mm});
            skCircle(sketch, "E387", {"center": v(-3675.09, 3232.1) * mm, "radius": 40 * mm});
            skCircle(sketch, "E388", {"center": v(-4213.06, 3753) * mm, "radius": 40 * mm});
            skCircle(sketch, "E389", {"center": v(-5167.65, 2798.4) * mm, "radius": 40 * mm});
            skCircle(sketch, "E390", {"center": v(-2137.34, -1749.5) * mm, "radius": 40 * mm});
            skCircle(sketch, "E391", {"center": v(-1558.95, -1749.5) * mm, "radius": 40 * mm});
            skCircle(sketch, "E392", {"center": v(-958.95, -1749.5) * mm, "radius": 40 * mm});
            skCircle(sketch, "E393", {"center": v(941.05, -1749.5) * mm, "radius": 40 * mm});
            skCircle(sketch, "E394", {"center": v(1541.05, -1749.5) * mm, "radius": 40 * mm});
            skCircle(sketch, "E395", {"center": v(2119.43, -1749.5) * mm, "radius": 40 * mm});
            skCircle(sketch, "E396", {"center": v(2671.86, -1114.52) * mm, "radius": 40 * mm});
            skCircle(sketch, "E397", {"center": v(2671.46, -508.68) * mm, "radius": 40 * mm});
            skCircle(sketch, "E398", {"center": v(4098.03, -1115.66) * mm, "radius": 40 * mm});
            skCircle(sketch, "E399", {"center": v(4098.03, 234.34) * mm, "radius": 40 * mm});
            skCircle(sketch, "E400", {"center": v(4098.03, 885.71) * mm, "radius": 40 * mm});
            skCircle(sketch, "E401", {"center": v(2681.11, 1401.97) * mm, "radius": 40 * mm});
            skCircle(sketch, "E402", {"center": v(2681.11, 2001.97) * mm, "radius": 40 * mm});
            skCircle(sketch, "E403", {"center": v(4098.03, 2235.71) * mm, "radius": 40 * mm});
            skCircle(sketch, "E404", {"center": v(2119.43, 2653.44) * mm, "radius": 40 * mm});
            skCircle(sketch, "E405", {"center": v(1541.05, 2653.44) * mm, "radius": 40 * mm});
            skCircle(sketch, "E406", {"center": v(941.05, 2653.44) * mm, "radius": 40 * mm});
            skCircle(sketch, "E407", {"center": v(-958.95, 2653.44) * mm, "radius": 40 * mm});
            skCircle(sketch, "E408", {"center": v(-1558.95, 2653.44) * mm, "radius": 40 * mm});
            skCircle(sketch, "E409", {"center": v(-2158.94, 2653.14) * mm, "radius": 40 * mm});
            skCircle(sketch, "E410", {"center": v(-2699.02, 2001.97) * mm, "radius": 40 * mm});
            skCircle(sketch, "E411", {"center": v(-2699.02, 1401.97) * mm, "radius": 40 * mm});
            skCircle(sketch, "E412", {"center": v(-2699.02, -1098.03) * mm, "radius": 40 * mm});
            skCircle(sketch, "E413", {"center": v(-2699.02, -498.03) * mm, "radius": 40 * mm});
            skCircle(sketch, "E414", {"center": v(3254.05, -3932.39) * mm, "radius": 40 * mm});
            skCircle(sketch, "E415", {"center": v(2716.08, -3411.5) * mm, "radius": 40 * mm});
            skCircle(sketch, "E416", {"center": v(2299.45, -4886.98) * mm, "radius": 40 * mm});
            skCircle(sketch, "E417", {"center": v(1761.49, -4366.09) * mm, "radius": 40 * mm});
            skSolve(sketch);
        }
        {
            var Q0;
            Q0 = qSketchRegion(id + "F23", true);
            extrude(context, id + "F24", {"entities" : qUnion([Q0]), "depth" : 460 * mm, "offsetDistance" : 25 * mm});
        }
        {
            var Q0;
            Q0=makeQuery(id+"F8.opExtrude","CAP_FACE",FACE,{"disambiguationData":[OSD([sQuery(id+"F7.wireOp",EDGE,"E263.0.0"),sQuery(id+"F7.wireOp",EDGE,"E263.0.1"),sQuery(id+"F7.wireOp",EDGE,"E263.0.2"),sQuery(id+"F7.wireOp",EDGE,"E263.0.3"),sQuery(id+"F7.wireOp",EDGE,"E263.0.4"),sQuery(id+"F7.wireOp",EDGE,"E263.0.5"),sQuery(id+"F7.wireOp",EDGE,"E263.0.6"),sQuery(id+"F7.wireOp",EDGE,"E263.0.7"),sQuery(id+"F7.wireOp",EDGE,"E263.0.8"),sQuery(id+"F7.wireOp",EDGE,"E263.0.9"),sQuery(id+"F7.wireOp",EDGE,"E263.0.10"),sQuery(id+"F7.wireOp",EDGE,"E263.0.11"),sQuery(id+"F7.wireOp",EDGE,"E263.0.12"),sQuery(id+"F7.wireOp",EDGE,"E263.0.13"),sQuery(id+"F7.wireOp",EDGE,"E263.0.14"),sQuery(id+"F7.wireOp",EDGE,"E263.0.15"),sQuery(id+"F7.wireOp",EDGE,"E263.0.16"),sQuery(id+"F7.wireOp",EDGE,"E263.0.17"),sQuery(id+"F7.wireOp",EDGE,"E263.0.18"),sQuery(id+"F7.wireOp",EDGE,"E263.0.19"),sQuery(id+"F7.wireOp",EDGE,"E263.0.20"),sQuery(id+"F7.wireOp",EDGE,"E263.0.21")])],"isStart":true});
            var Q1;
            Q1=makeQuery(id+"F8.opExtrude","SWEPT_FACE",FACE,{"disambiguationData":[OSD([sQuery(id+"F7.wireOp",EDGE,"E263.0.19")])]});
            var Q2;
            Q2=makeQuery(id+"F8.opExtrude","SWEPT_FACE",FACE,{"disambiguationData":[OSD([sQuery(id+"F7.wireOp",EDGE,"E263.0.2")])]});
            var Q3;
            Q3=makeQuery(id+"F8.opExtrude","SWEPT_FACE",FACE,{"disambiguationData":[OSD([sQuery(id+"F7.wireOp",EDGE,"E263.0.13")])]});
            var Q4;
            Q4=makeQuery(id+"F8.opExtrude","SWEPT_FACE",FACE,{"disambiguationData":[OSD([sQuery(id+"F7.wireOp",EDGE,"E263.0.8")])]});
            fillet(context, id + "F25", {"entities" : qUnion([Q0, Q1, Q2, Q3, Q4]), "radius" : 3 * mm, "tangentPropagation" : true, "allowEdgeOverflow" : false});
        }
        {
            var Q0;
            Q0=makeQuery(id+"F14.opExtrude","CAP_EDGE",EDGE,{"disambiguationData":[OSD([sQuery(id+"F13.wireOp",EDGE,"E269.0.4"),sQuery(id+"F13.wireOp",EDGE,"E269.0.5")])],"isStart":true});
            var Q1;
            Q1=makeQuery(id+"F14.opExtrude","CAP_EDGE",EDGE,{"disambiguationData":[OSD([sQuery(id+"F13.wireOp",EDGE,"E269.0.6")])],"isStart":true});
            var Q2;
            Q2=makeQuery(id+"F14.opExtrude","CAP_EDGE",EDGE,{"disambiguationData":[OSD([sQuery(id+"F13.wireOp",EDGE,"E272.0.3"),sQuery(id+"F13.wireOp",EDGE,"E272.0.4")])],"isStart":true});
            var Q3;
            Q3=makeQuery(id+"F14.opExtrude","CAP_EDGE",EDGE,{"disambiguationData":[OSD([sQuery(id+"F13.wireOp",EDGE,"E272.0.2")])],"isStart":true});
            var Q4;
            Q4=makeQuery(id+"F14.opExtrude","CAP_EDGE",EDGE,{"disambiguationData":[OSD([sQuery(id+"F13.wireOp",EDGE,"E271.0.3")])],"isStart":true});
            var Q5;
            Q5=makeQuery(id+"F14.opExtrude","CAP_EDGE",EDGE,{"disambiguationData":[OSD([sQuery(id+"F13.wireOp",EDGE,"E271.0.1"),sQuery(id+"F13.wireOp",EDGE,"E271.0.2")])],"isStart":true});
            var Q6;
            Q6=makeQuery(id+"F14.opExtrude","CAP_EDGE",EDGE,{"disambiguationData":[OSD([sQuery(id+"F13.wireOp",EDGE,"E270.0.0"),sQuery(id+"F13.wireOp",EDGE,"E270.0.7")])],"isStart":true});
            var Q7;
            Q7=makeQuery(id+"F14.opExtrude","CAP_EDGE",EDGE,{"disambiguationData":[OSD([sQuery(id+"F13.wireOp",EDGE,"E270.0.6")])],"isStart":true});
            fillet(context, id + "F26", {"entities" : qUnion([Q0, Q1, Q2, Q3, Q4, Q5, Q6, Q7]), "radius" : 5 * mm, "tangentPropagation" : true, "allowEdgeOverflow" : false});
        }
    });
